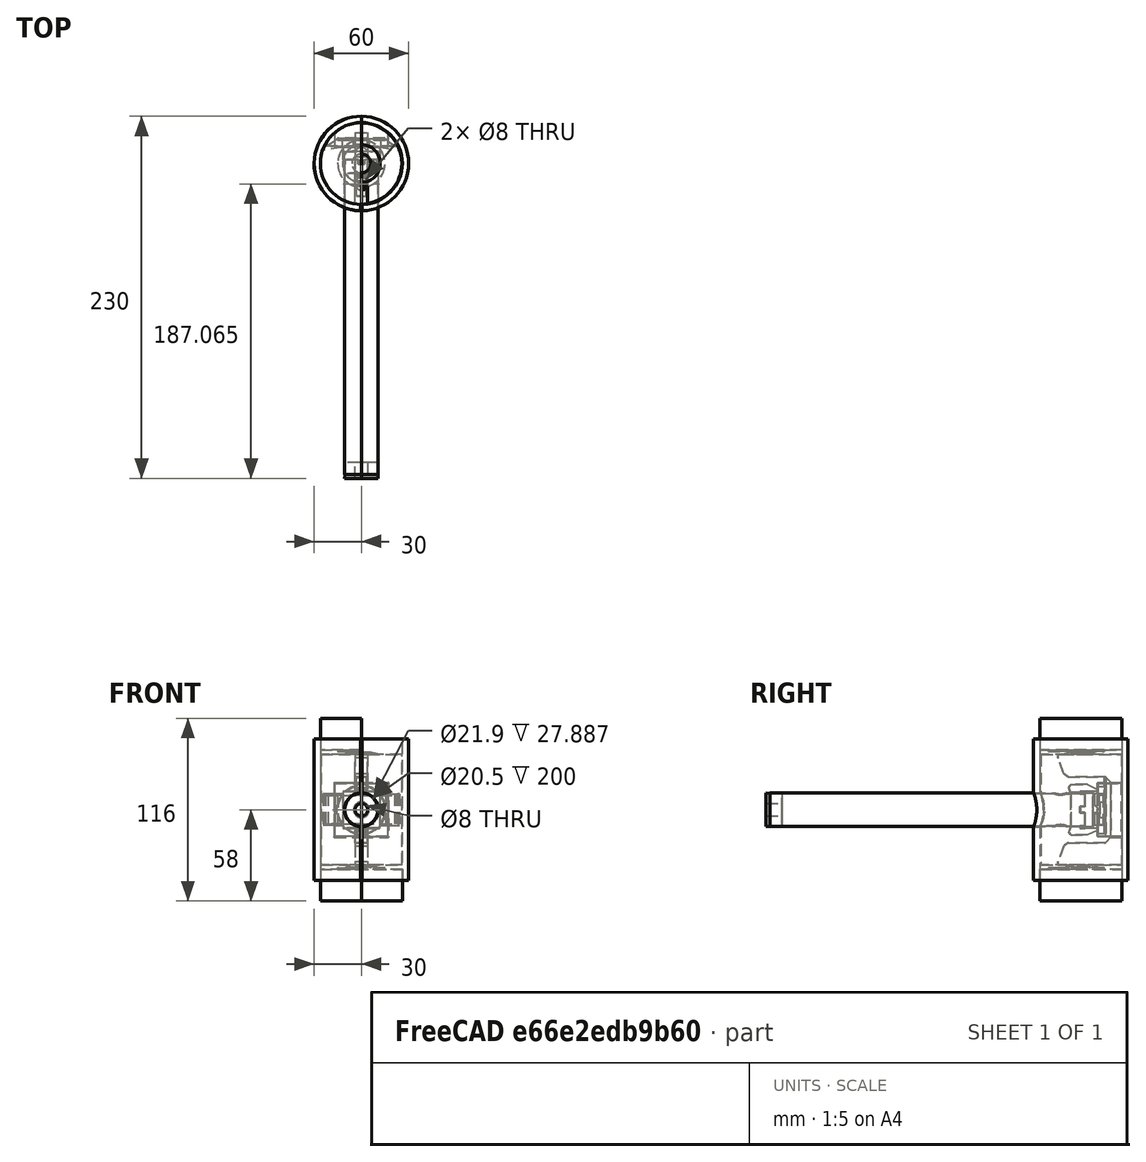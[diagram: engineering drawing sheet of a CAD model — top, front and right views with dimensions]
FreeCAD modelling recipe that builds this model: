
FCSTD DOCUMENT  (FreeCAD 0.21R33771 (Git))
Label: HammerWithDrawings
License: All rights reserved
LicenseURL: https://en.wikipedia.org/wiki/All_rights_reserved
objects: TechDraw::DrawViewDimension×57, Sketcher::SketchObject×26, TechDraw::DrawProjGroupItem×16, PartDesign::Pad×13, PartDesign::Pocket×13, PartDesign::Body×13, App::Link×13, PartDesign::Chamfer×7, TechDraw::DrawSVGTemplate×4, TechDraw::DrawProjGroup×4, TechDraw::DrawPage×4, PartDesign::FeatureBase×3, TechDraw::DrawViewSection×3, PartDesign::AdditiveCone×2, PartDesign::Fillet×2, Spreadsheet::Sheet×1, TechDraw::DrawViewDetail×1, PartDesign::Draft×1, App::DocumentObjectGroupPython×1, Part::FeaturePython×1, +3 more types
note: 216 computed .brp shape members not serialized (recipe doc carries the construction recipe); baked Part::Feature solids carry a one-line shape summary decoded from their .brp

FEATURE [Spreadsheet::Sheet] Spreadsheet  label="Properties"
  cells = A1='PropertyName; B1='Value; A2='Handle_OD; B2(Handle_OD)=21.5; A3='Head_ID; B3(Head_ID)=51.4; A4='Head_Len; B4(Handle_Len)=110; A5='Clearance; B5(Clearance)=0.2; A6='Inset_Len; B6(Insert_Len)=70; A7='Sensor_Wire_Track_Width; B7(Sensor_Wire_Track_Width)=8; A8='Spring_Plate_Len; B8(Spring_Plate_Len)=46; A9='Sensor_Diameter; B9(Sensor_Diameter)=30; A10='Handle_ID; B10(Handle_ID)=20.5
FEATURE [Sketcher::SketchObject] Sketch  label="base"
  FullyConstrained = true
  MapMode = 5
  Support = -> [XY_Plane001]
  expr: Constraints[1] = <<Properties>>.Head_ID
  sketch-geometry (1):
    g0: Circle CenterX=0 CenterY=0 CenterZ=0 NormalX=0 NormalY=0 NormalZ=1 AngleXU=0 Radius=25.7
  constraints (2):
    c: Coincident(g0,g-1)
    c: Diameter(g0) = 51.4
FEATURE [PartDesign::Pad] Pad  label="Base"
  Direction = (0,0,1)
  Length = 35
  Length2 = 35
  Profile = -> Sketch
  ReferenceAxis = -> Sketch [N_Axis]
  Type = 4
  expr: Length = <<Properties>>.Insert_Len / 2
  expr: Length2 = <<Properties>>.Insert_Len / 2
FEATURE [Sketcher::SketchObject] Sketch001  label="sensor_wire_slot"
  FullyConstrained = true
  MapMode = 5
  Support = -> [XY_Plane001]
  expr: Constraints[11] = <<Properties>>.Sensor_Wire_Track_Width
  expr: Constraints[1] = Sketch.Constraints[1]
  sketch-geometry (7):
    g0: Circle CenterX=0 CenterY=0 CenterZ=0 NormalX=0 NormalY=0 NormalZ=1 AngleXU=0 Radius=25.7
    g1: LineSegment StartX=-4 StartY=-25.3868 StartZ=0 EndX=-4 EndY=-14.4568 EndZ=0
    g2: LineSegment StartX=-4 StartY=-14.4568 StartZ=0 EndX=4 EndY=-14.4568 EndZ=0
    g3: LineSegment StartX=4 StartY=-14.4568 StartZ=0 EndX=4 EndY=-25.3868 EndZ=0
    g4: ArcOfCircle CenterX=0 CenterY=0 CenterZ=0 NormalX=0 NormalY=0 NormalZ=1 AngleXU=0 Radius=25.7 StartAngle=4.55611 EndAngle=4.86867
    g5: GeomPoint X=0 Y=-14.4568 Z=0
    g6: Circle CenterX=0 CenterY=0 CenterZ=0 NormalX=0 NormalY=0 NormalZ=1 AngleXU=0 Radius=15
  constraints (17):
    c: Coincident(g0,g-1)
    c: Diameter(g0) = 51.4
    c: Vertical(g1)
    c: Coincident(g2,g1)
    c: Horizontal(g2)
    c: Coincident(g3,g2)
    c: Vertical(g3)
    c: Coincident(g4,g0)
    c: Coincident(g4,g1)
    c: Coincident(g4,g3)
    c: PointOnObject(g3,g0)
    c: DistanceX(g2,g2) = 8
    c: Symmetric(g2,g2,g5)
    c: PointOnObject(g5,g-2)
    c: Coincident(g6,g4)
    c: Diameter(g6) = 30
    c: PointOnObject(g2,g6)
FEATURE [PartDesign::Pocket] Pocket  label="Sensor_Wire_Slot"
  BaseFeature = -> Pad
  Direction = (0,0,-1)
  Length = 35
  Length2 = 35
  Profile = -> Sketch001
  ReferenceAxis = -> Sketch001 [N_Axis]
  Type = 4
  expr: Length = <<Properties>>.Insert_Len / 2
  expr: Length2 = <<Properties>>.Insert_Len / 2
FEATURE [Sketcher::SketchObject] Sketch002  label="handle_hole"
  FullyConstrained = true
  MapMode = 5
  Placement = pos=(0,0,0) rot=(1,0,0;1.5708rad)
  Support = -> [XZ_Plane001]
  expr: Constraints[1] = <<Properties>>.Handle_OD + <<Properties>>.Clearance * 2
  sketch-geometry (1):
    g0: Circle CenterX=0 CenterY=0 CenterZ=0 NormalX=0 NormalY=0 NormalZ=1 AngleXU=0 Radius=10.95
  constraints (2):
    c: Coincident(g0,g-1)
    c: Diameter(g0) = 21.9
FEATURE [PartDesign::Pocket] Pocket001  label="Handle_hole"
  BaseFeature = -> Pocket
  Direction = (0,1,2e-16)
  Length = 25.7
  Length2 = 25.7
  Profile = -> Sketch002
  ReferenceAxis = -> Sketch002 [N_Axis]
  Type = 4
  expr: Length = <<Properties>>.Head_ID / 2
  expr: Length2 = <<Properties>>.Head_ID / 2
FEATURE [Sketcher::SketchObject] Sketch004  label="top_sensor_hole"
  FullyConstrained = true
  MapMode = 5
  Placement = pos=(0,0,0) rot=(0.57735,0.57735,0.57735;2.0944rad)
  Support = -> [YZ_Plane001]
  expr: Constraints[20] = <<Properties>>.Head_ID
  expr: Constraints[7] = <<Properties>>.Sensor_Diameter + 4
  sketch-geometry (9):
    g0: LineSegment StartX=-25.7 StartY=-17 StartZ=0 EndX=-25.7 EndY=17 EndZ=0
    g1: LineSegment StartX=25.7 StartY=17 StartZ=0 EndX=25.7 EndY=-17 EndZ=0
    g2: LineSegment StartX=25.7 StartY=-17 StartZ=0 EndX=-25.7 EndY=-17 EndZ=0
    g3: GeomPoint X=0 Y=0 Z=0
    g4: LineSegment StartX=10.5 StartY=17 StartZ=0 EndX=25.7 EndY=17 EndZ=0
    g5: LineSegment StartX=25.7 StartY=17 StartZ=0 EndX=25.7 EndY=-17 EndZ=0
    g6: LineSegment StartX=25.7 StartY=-17 StartZ=0 EndX=10.5 EndY=-17 EndZ=0
    g7: LineSegment StartX=10.5 StartY=-17 StartZ=0 EndX=10.5 EndY=17 EndZ=0
    g8: LineSegment StartX=-25.7 StartY=17 StartZ=0 EndX=25.7 EndY=17 EndZ=0
  constraints (23):
    c: Coincident(g1,g2)
    c: Coincident(g2,g0)
    c: Horizontal(g2)
    c: Vertical(g0)
    c: Vertical(g1)
    c: Symmetric(g1,g0,g3)
    c: Coincident(g3,g-1)
    c: DistanceY(g1,g1) = 34
    c: Coincident(g4,g5)
    c: Coincident(g5,g6)
    c: Coincident(g6,g7)
    c: Horizontal(g4)
    c: Horizontal(g6)
    c: Vertical(g5)
    c: Vertical(g7)
    c: PointOnObject(g5,g2)
    c: Coincident(g7,g4)
    c: Coincident(g8,g0)
    c: Coincident(g8,g1)
    c: Horizontal(g8)
    c: DistanceX(g8,g8) = 51.4
    c: Coincident(g4,g1)
    c: DistanceX(g3,g4) = 10.5
FEATURE [PartDesign::Pocket] Pocket002  label="Top_Sensor_Hole"
  BaseFeature = -> Pocket001
  Direction = (-1,2e-16,-3e-16)
  Length = 17
  Length2 = 17
  Profile = -> Sketch004
  ReferenceAxis = -> Sketch004 [N_Axis]
  Type = 4
  expr: Length = <<Properties>>.Sensor_Diameter / 2 + 2
  expr: Length2 = <<Properties>>.Sensor_Diameter / 2 + 2
FEATURE [PartDesign::Chamfer] Chamfer
  Angle = 70
  Base = -> Pocket002 [Edge30,Edge32]
  BaseFeature = -> Pocket002
  ChamferType = 2
  FlipDirection = false
  Size = 8
  Size2 = 1
  SupportTransform = false
  UseAllEdges = false
FEATURE [Sketcher::SketchObject] Sketch003  label="spring_plate_slot"
  FullyConstrained = true
  MapMode = 5
  Support = -> [XY_Plane001]
  expr: Constraints[1] = Sketch.Constraints[1]
  expr: Constraints[3] = <<Properties>>.Sensor_Diameter + <<Properties>>.Clearance * 2
  expr: Constraints[7] = <<Properties>>.Spring_Plate_Len
  sketch-geometry (15):
    g0: Circle CenterX=0 CenterY=0 CenterZ=0 NormalX=0 NormalY=0 NormalZ=1 AngleXU=0 Radius=25.7
    g1: LineSegment StartX=-15.2 StartY=15.4669 StartZ=0 EndX=15.2 EndY=15.4669 EndZ=0
    g2: GeomPoint X=0 Y=15.4669 Z=0
    g3: LineSegment StartX=-23 StartY=11.4669 StartZ=0 EndX=23 EndY=11.4669 EndZ=0
    g4: GeomPoint X=0 Y=11.4669 Z=0
    g5: LineSegment StartX=-15.2 StartY=15.4669 StartZ=0 EndX=-21 EndY=11.4669 EndZ=0
    g6: LineSegment StartX=15.2 StartY=15.4669 StartZ=0 EndX=21 EndY=11.4669 EndZ=0
    g7: LineSegment StartX=21 StartY=11.4669 StartZ=0 EndX=23 EndY=11.4669 EndZ=0
    g8: LineSegment StartX=-21 StartY=11.4669 StartZ=0 EndX=-23 EndY=11.4669 EndZ=0
    g9: ArcOfCircle CenterX=0 CenterY=0 CenterZ=0 NormalX=0 NormalY=0 NormalZ=1 AngleXU=0 Radius=25.7 StartAngle=2.6791 EndAngle=2.80587
    g10: ArcOfCircle CenterX=0 CenterY=0 CenterZ=0 NormalX=0 NormalY=0 NormalZ=1 AngleXU=0 Radius=25.7 StartAngle=0.335723 EndAngle=0.462496
    g11: LineSegment StartX=-11 StartY=10.5 StartZ=0 EndX=-24.2652 EndY=8.46691 EndZ=0
    g12: LineSegment StartX=11 StartY=10.5 StartZ=0 EndX=24.2652 EndY=8.46691 EndZ=0
    g13: LineSegment StartX=11 StartY=10.5 StartZ=0 EndX=-11 EndY=10.5 EndZ=0
    g14: GeomPoint X=0 Y=10.5 Z=0
  constraints (39):
    c: Coincident(g0,g-1)
    c: Diameter(g0) = 51.4
    c: Horizontal(g1)
    c: DistanceX(g1,g1) = 30.4
    c: Symmetric(g1,g1,g2)
    c: PointOnObject(g2,g-2)
    c: Horizontal(g3)
    c: DistanceX(g3,g3) = 46
    c: Symmetric(g3,g3,g4)
    c: PointOnObject(g4,g-2)
    c: Coincident(g5,g1)
    c: PointOnObject(g5,g3)
    c: Coincident(g6,g1)
    c: PointOnObject(g6,g3)
    c: Coincident(g7,g6)
    c: PointOnObject(g7,g0)
    c: Horizontal(g7)
    c: Coincident(g8,g5)
    c: PointOnObject(g8,g0)
    c: Horizontal(g8)
    c: Equal(g8,g7)
    c: PointOnObject(g3,g0)
    c: DistanceY(g6,g1) = 4
    c: DistanceX(g6,g7) = 2
    c: Coincident(g9,g0)
    c: Coincident(g9,g8)
    c: Coincident(g10,g9)
    c: Coincident(g10,g7)
    c: Coincident(g13,g12)
    c: Coincident(g13,g11)
    c: Horizontal(g13)
    c: Coincident(g10,g12)
    c: Coincident(g9,g11)
    c: DistanceX(g12,g6) = 10
    c: Equal(g12,g11)
    c: DistanceY(g10,g7) = 3
    c: Symmetric(g13,g13,g14)
    c: PointOnObject(g14,g-2)
    c: DistanceY(g9,g14) = 10.5
FEATURE [PartDesign::Pocket] Pocket003  label="Spring_Plate_Slot"
  BaseFeature = -> Chamfer
  Direction = (0,0,-1)
  Length = 10
  Length2 = 10
  Profile = -> Sketch003
  ReferenceAxis = -> Sketch003 [N_Axis]
  Type = 4
FEATURE [PartDesign::Chamfer] Chamfer001
  Angle = 45
  Base = -> Pocket003 [Edge43,Edge46,Edge45,Edge47,Edge44,Edge42]
  BaseFeature = -> Pocket003
  ChamferType = 0
  FlipDirection = false
  Size = 0.5
  Size2 = 1
  SupportTransform = false
  UseAllEdges = false
FEATURE [Sketcher::SketchObject] Sketch005  label="top_sens_base"
  FullyConstrained = true
  MapMode = 5
  Support = -> [XY_Plane]
  expr: Constraints[18] = <<Properties>>.Clearance
  expr: Constraints[1] = <<Properties>>.Head_ID
  expr: Constraints[3] = 34 - <<Properties>>.Clearance * 2
  expr: Constraints[6] = 10.5 + <<Properties>>.Clearance
  sketch-geometry (8):
    g0: Circle CenterX=0 CenterY=0 CenterZ=0 NormalX=0 NormalY=0 NormalZ=1 AngleXU=0 Radius=25.7
    g1: LineSegment StartX=-16.8 StartY=10.7 StartZ=0 EndX=16.8 EndY=10.7 EndZ=0
    g2: GeomPoint X=0 Y=10.7 Z=0
    g3: LineSegment StartX=-16.8 StartY=10.7 StartZ=0 EndX=-16.8 EndY=19.1836 EndZ=0
    g4: LineSegment StartX=16.8 StartY=10.7 StartZ=0 EndX=16.8 EndY=19.1836 EndZ=0
    g5: GeomPoint X=0 Y=25.7 Z=0
    g6: ArcOfCircle CenterX=0 CenterY=0 CenterZ=0 NormalX=0 NormalY=0 NormalZ=1 AngleXU=0 Radius=25.5 StartAngle=0.851542 EndAngle=2.29005
    g7: GeomPoint X=0 Y=25.5 Z=0
  constraints (19):
    c: Coincident(g0,g-1)
    c: Diameter(g0) = 51.4
    c: Horizontal(g1)
    c: DistanceX(g1,g1) = 33.6
    c: Symmetric(g1,g1,g2)
    c: PointOnObject(g2,g-2)
    c: DistanceY(g0,g2) = 10.7
    c: Coincident(g3,g1)
    c: Vertical(g3)
    c: Vertical(g4)
    c: Coincident(g4,g1)
    c: PointOnObject(g5,g0)
    c: PointOnObject(g5,g-2)
    c: Coincident(g6,g0)
    c: Coincident(g6,g3)
    c: Coincident(g6,g4)
    c: PointOnObject(g7,g6)
    c: PointOnObject(g7,g-2)
    c: DistanceY(g7,g5) = 0.2
FEATURE [PartDesign::Pad] Pad001  label="Top_Base"
  Direction = (0,0,1)
  Length = 16.8
  Length2 = 16.8
  Profile = -> Sketch005
  ReferenceAxis = -> Sketch005 [N_Axis]
  Type = 4
  expr: Length = <<Properties>>.Sensor_Diameter / 2 + 2 - <<Properties>>.Clearance
  expr: Length2 = <<Properties>>.Sensor_Diameter / 2 + 2 - <<Properties>>.Clearance
FEATURE [Sketcher::SketchObject] Sketch006
  FullyConstrained = true
  MapMode = 5
  Support = -> [XY_Plane]
  expr: Constraints[1] = Sketch003.Constraints[1]
  expr: Constraints[22] = Sketch003.Constraints[22]
  expr: Constraints[23] = Sketch003.Constraints[23]
  expr: Constraints[33] = Sketch003.Constraints[33]
  expr: Constraints[35] = Sketch003.Constraints[35]
  expr: Constraints[38] = Sketch003.Constraints[38]
  expr: Constraints[3] = Sketch003.Constraints[3]
  expr: Constraints[7] = Sketch003.Constraints[7]
  sketch-geometry (15):
    g0: Circle CenterX=0 CenterY=0 CenterZ=0 NormalX=0 NormalY=0 NormalZ=1 AngleXU=0 Radius=25.7
    g1: LineSegment StartX=-15.2 StartY=15.4669 StartZ=0 EndX=15.2 EndY=15.4669 EndZ=0
    g2: GeomPoint X=0 Y=15.4669 Z=0
    g3: LineSegment StartX=-23 StartY=11.4669 StartZ=0 EndX=23 EndY=11.4669 EndZ=0
    g4: GeomPoint X=0 Y=11.4669 Z=0
    g5: LineSegment StartX=-15.2 StartY=15.4669 StartZ=0 EndX=-21 EndY=11.4669 EndZ=0
    g6: LineSegment StartX=15.2 StartY=15.4669 StartZ=0 EndX=21 EndY=11.4669 EndZ=0
    g7: LineSegment StartX=21 StartY=11.4669 StartZ=0 EndX=23 EndY=11.4669 EndZ=0
    g8: LineSegment StartX=-21 StartY=11.4669 StartZ=0 EndX=-23 EndY=11.4669 EndZ=0
    g9: ArcOfCircle CenterX=0 CenterY=0 CenterZ=0 NormalX=0 NormalY=0 NormalZ=1 AngleXU=0 Radius=25.7 StartAngle=2.6791 EndAngle=2.80587
    g10: ArcOfCircle CenterX=0 CenterY=0 CenterZ=0 NormalX=0 NormalY=0 NormalZ=1 AngleXU=0 Radius=25.7 StartAngle=0.335723 EndAngle=0.462496
    g11: LineSegment StartX=-11 StartY=10.5 StartZ=0 EndX=-24.2652 EndY=8.46691 EndZ=0
    g12: LineSegment StartX=11 StartY=10.5 StartZ=0 EndX=24.2652 EndY=8.46691 EndZ=0
    g13: LineSegment StartX=11 StartY=10.5 StartZ=0 EndX=-11 EndY=10.5 EndZ=0
    g14: GeomPoint X=0 Y=10.5 Z=0
  constraints (40):
    c: Coincident(g0,g-1)
    c: Diameter(g0) = 51.4
    c: Horizontal(g1)
    c: DistanceX(g1,g1) = 30.4
    c: Symmetric(g1,g1,g2)
    c: PointOnObject(g2,g-2)
    c: Horizontal(g3)
    c: DistanceX(g3,g3) = 46
    c: Symmetric(g3,g3,g4)
    c: PointOnObject(g4,g-2)
    c: Coincident(g5,g1)
    c: PointOnObject(g5,g3)
    c: Coincident(g6,g1)
    c: PointOnObject(g6,g3)
    c: Coincident(g7,g6)
    c: PointOnObject(g7,g0)
    c: Horizontal(g7)
    c: Coincident(g8,g5)
    c: PointOnObject(g8,g0)
    c: Horizontal(g8)
    c: Equal(g8,g7)
    c: PointOnObject(g3,g0)
    c: DistanceY(g6,g1) = 4
    c: DistanceX(g6,g7) = 2
    c: Coincident(g9,g0)
    c: Coincident(g9,g8)
    c: Coincident(g10,g9)
    c: Coincident(g10,g7)
    c: Coincident(g13,g12)
    c: Coincident(g13,g11)
    c: Horizontal(g13)
    c: Coincident(g10,g12)
    c: Coincident(g9,g11)
    c: DistanceX(g12,g6) = 10
    c: Equal(g12,g11)
    c: DistanceY(g10,g7) = 3
    c: Symmetric(g13,g13,g14)
    c: PointOnObject(g14,g-2)
    c: DistanceY(g9,g14) = 10.5
    c: DistanceY(g9,g2) = 15.4669
FEATURE [PartDesign::Pocket] Pocket004
  BaseFeature = -> Pad001
  Direction = (0,0,-1)
  Length = 9.5
  Length2 = 9.5
  Profile = -> Sketch006
  ReferenceAxis = -> Sketch006 [N_Axis]
  Type = 4
FEATURE [PartDesign::Chamfer] Chamfer002
  Angle = 45
  Base = -> Pocket004 [Edge22,Edge12]
  BaseFeature = -> Pocket004
  ChamferType = 0
  FlipDirection = false
  Size = 0.3
  Size2 = 1
  SupportTransform = false
  UseAllEdges = false
FEATURE [Sketcher::SketchObject] Sketch007
  FullyConstrained = true
  MapMode = 5
  Placement = pos=(0,0,0) rot=(1,0,0;1.5708rad)
  Support = -> [XZ_Plane]
  expr: Constraints[11] = <<Properties>>.Sensor_Wire_Track_Width
  expr: Constraints[1] = <<Properties>>.Sensor_Diameter + 1
  expr: Constraints[27] = <<Properties>>.Sensor_Wire_Track_Width
  sketch-geometry (11):
    g0: Circle CenterX=0 CenterY=0 CenterZ=0 NormalX=0 NormalY=0 NormalZ=1 AngleXU=0 Radius=15.5
    g1: LineSegment StartX=-4 StartY=14.975 StartZ=0 EndX=-4 EndY=27.305 EndZ=0
    g2: LineSegment StartX=-4 StartY=27.305 StartZ=0 EndX=4 EndY=27.305 EndZ=0
    g3: LineSegment StartX=4 StartY=27.305 StartZ=0 EndX=4 EndY=14.975 EndZ=0
    g4: GeomPoint X=0 Y=27.305 Z=0
    g5: LineSegment StartX=-4 StartY=-14.975 StartZ=0 EndX=-4 EndY=-27.305 EndZ=0
    g6: LineSegment StartX=-4 StartY=-27.305 StartZ=0 EndX=4 EndY=-27.305 EndZ=0
    g7: LineSegment StartX=4 StartY=-27.305 StartZ=0 EndX=4 EndY=-14.975 EndZ=0
    g8: GeomPoint X=0 Y=-27.305 Z=0
    g9: ArcOfCircle CenterX=0 CenterY=0 CenterZ=0 NormalX=0 NormalY=0 NormalZ=1 AngleXU=0 Radius=15.5 StartAngle=1.83181 EndAngle=4.45137
    g10: ArcOfCircle CenterX=0 CenterY=0 CenterZ=0 NormalX=0 NormalY=0 NormalZ=1 AngleXU=0 Radius=15.5 StartAngle=4.97341 EndAngle=7.59296
  constraints (28):
    c: Coincident(g0,g-1)
    c: Diameter(g0) = 31
    c: PointOnObject(g1,g0)
    c: Vertical(g1)
    c: Coincident(g2,g1)
    c: Horizontal(g2)
    c: Coincident(g3,g2)
    c: PointOnObject(g3,g0)
    c: Vertical(g3)
    c: Symmetric(g2,g2,g4)
    c: PointOnObject(g4,g-2)
    c: DistanceX(g2,g2) = 8
    c: DistanceY(g3,g3) = 12.33
    c: Vertical(g5)
    c: Coincident(g6,g5)
    c: Horizontal(g6)
    c: Coincident(g7,g6)
    c: Vertical(g7)
    c: Symmetric(g6,g6,g8)
    c: PointOnObject(g8,g-2)
    c: Equal(g7,g3)
    c: Coincident(g9,g0)
    c: Coincident(g9,g1)
    c: Coincident(g9,g5)
    c: Coincident(g10,g9)
    c: Coincident(g10,g3)
    c: Coincident(g10,g7)
    c: DistanceX(g6,g6) = 8
FEATURE [PartDesign::Pocket] Pocket005
  BaseFeature = -> Chamfer002
  Direction = (0,1,2e-16)
  Length = 0
  Length2 = 5
  Offset = 0.4
  Profile = -> Sketch007
  ReferenceAxis = -> Sketch007 [N_Axis]
  Type = 3
  UpToFace = -> Chamfer002 [Face11]
FEATURE [PartDesign::Body] Body001  label="TopSensor"
  Group = -> [Sketch005,Pad001,Sketch006,Pocket004,Chamfer002,Sketch007,Pocket005]
  Origin = -> Origin
  Tip = -> Pocket005
FEATURE [Sketcher::SketchObject] Sketch008
  FullyConstrained = true
  MapMode = 5
  Placement = pos=(0,0,0) rot=(0.57735,0.57735,0.57735;2.0944rad)
  Support = -> [YZ_Plane001]
  expr: Constraints[16] = <<Properties>>.Sensor_Diameter + 2
  sketch-geometry (14):
    g0: LineSegment StartX=15.5 StartY=21 StartZ=0 EndX=15.5 EndY=-21 EndZ=0
    g1: LineSegment StartX=15.5 StartY=-21 StartZ=0 EndX=-19.02 EndY=-21 EndZ=0
    g2: LineSegment StartX=-19.02 StartY=-21 StartZ=0 EndX=-19.02 EndY=-16 EndZ=0
    g3: LineSegment StartX=-19.02 StartY=-16 StartZ=0 EndX=10.5 EndY=-16 EndZ=0
    g4: LineSegment StartX=10.5 StartY=-16 StartZ=0 EndX=10.5 EndY=16 EndZ=0
    g5: LineSegment StartX=10.5 StartY=16 StartZ=0 EndX=-19.02 EndY=16 EndZ=0
    g6: LineSegment StartX=-19.02 StartY=16 StartZ=0 EndX=-19.02 EndY=21 EndZ=0
    g7: LineSegment StartX=-19.02 StartY=21 StartZ=0 EndX=15.5 EndY=21 EndZ=0
    g8: GeomPoint X=10.5 Y=0 Z=0
    g9: GeomPoint X=15.5 Y=0 Z=0
    g10: GeomPoint X=15.5 Y=21 Z=0
    g11: GeomPoint X=15.5 Y=-21 Z=0
    g12: GeomPoint X=10.5 Y=16 Z=0
    g13: GeomPoint X=10.5 Y=-16 Z=0
  constraints (30):
    c: Vertical(g0)
    c: Horizontal(g1)
    c: Coincident(g2,g1)
    c: Vertical(g2)
    c: Coincident(g3,g2)
    c: Horizontal(g3)
    c: Vertical(g4)
    c: Horizontal(g5)
    c: Coincident(g6,g5)
    c: Vertical(g6)
    c: Coincident(g7,g6)
    c: Horizontal(g7)
    c: Symmetric(g10,g11,g9)
    c: Symmetric(g13,g12,g8)
    c: PointOnObject(g8,g-1)
    c: PointOnObject(g9,g-1)
    c: DistanceY(g13,g12) = 32
    c: DistanceY(g6,g6) = 5
    c: DistanceX(g8,g9) = 5
    c: DistanceX(g-1,g8) = 10.5
    c: DistanceX(g7,g10) = 34.52
    c: Coincident(g0,g10)
    c: Coincident(g7,g0)
    c: Coincident(g4,g12)
    c: Coincident(g5,g4)
    c: Coincident(g0,g11)
    c: Coincident(g4,g13)
    c: Coincident(g3,g4)
    c: Coincident(g1,g0)
    c: Equal(g3,g5)
FEATURE [PartDesign::Pocket] Pocket006
  BaseFeature = -> Chamfer001
  Direction = (-1,2e-16,-3e-16)
  Length = 4
  Length2 = 4
  Profile = -> Sketch008
  ReferenceAxis = -> Sketch008 [N_Axis]
  Type = 4
  expr: Length = <<Properties>>.Sensor_Wire_Track_Width / 2
  expr: Length2 = <<Properties>>.Sensor_Wire_Track_Width / 2
FEATURE [PartDesign::Chamfer] Chamfer003
  Angle = 65
  Base = -> Pocket006 [Edge148,Edge154]
  BaseFeature = -> Pocket006
  ChamferType = 2
  FlipDirection = false
  Size = 3
  Size2 = 1
  SupportTransform = false
  UseAllEdges = false
FEATURE [PartDesign::Chamfer] Chamfer004
  Angle = 45
  Base = -> Chamfer003 [Edge167,Edge85,Edge52,Edge56]
  BaseFeature = -> Chamfer003
  ChamferType = 0
  FlipDirection = false
  Size = 2
  Size2 = 1
  SupportTransform = false
  UseAllEdges = false
FEATURE [PartDesign::Chamfer] Chamfer005
  Angle = 45
  Base = -> Chamfer004 [Edge169,Edge38]
  BaseFeature = -> Chamfer004
  ChamferType = 1
  FlipDirection = false
  Size = 4
  Size2 = 3.999
  SupportTransform = false
  UseAllEdges = false
FEATURE [Sketcher::SketchObject] Sketch009
  FullyConstrained = true
  MapMode = 5
  Support = -> [XY_Plane002]
  sketch-geometry (2):
    g0: Circle CenterX=0 CenterY=0 CenterZ=0 NormalX=0 NormalY=0 NormalZ=1 AngleXU=0 Radius=26
    g1: Circle CenterX=0 CenterY=0 CenterZ=0 NormalX=0 NormalY=0 NormalZ=1 AngleXU=0 Radius=30
  constraints (4):
    c: Coincident(g0,g-1)
    c: Coincident(g1,g0)
    c: Diameter(g0) = 52
    c: Diameter(g1) = 60
FEATURE [PartDesign::Pad] Pad002
  Direction = (0,0,1)
  Length = 45
  Length2 = 45
  Profile = -> Sketch009
  ReferenceAxis = -> Sketch009 [N_Axis]
  Type = 4
FEATURE [Sketcher::SketchObject] Sketch010
  FullyConstrained = true
  MapMode = 5
  Placement = pos=(0,0,0) rot=(1,0,0;1.5708rad)
  Support = -> [XZ_Plane002]
  expr: Constraints[1] = <<Properties>>.Handle_OD
  sketch-geometry (1):
    g0: Circle CenterX=0 CenterY=0 CenterZ=0 NormalX=0 NormalY=0 NormalZ=1 AngleXU=0 Radius=10.75
  constraints (2):
    c: Coincident(g0,g-1)
    c: Diameter(g0) = 21.5
FEATURE [PartDesign::Pocket] Pocket007
  BaseFeature = -> Pad002
  Direction = (0,1,2e-16)
  Length = 5
  Length2 = 5
  Profile = -> Sketch010
  ReferenceAxis = -> Sketch010 [N_Axis]
  Reversed = true
  Type = 1
FEATURE [Sketcher::SketchObject] Sketch011
  FullyConstrained = true
  MapMode = 5
  Placement = pos=(0,0,0) rot=(1,0,0;1.5708rad)
  Support = -> [XZ_Plane003]
  expr: Constraints[3] = <<Properties>>.Handle_ID
  sketch-geometry (2):
    g0: Circle CenterX=0 CenterY=0 CenterZ=0 NormalX=0 NormalY=0 NormalZ=1 AngleXU=0 Radius=10.625
    g1: Circle CenterX=0 CenterY=0 CenterZ=0 NormalX=0 NormalY=0 NormalZ=1 AngleXU=0 Radius=10.25
  constraints (4):
    c: Coincident(g0,g-1)
    c: Diameter(g0) = 21.25
    c: Coincident(g1,g0)
    c: Diameter(g1) = 20.5
FEATURE [PartDesign::Pad] Pad003
  Direction = (0,-1,-2e-16)
  Length = 200
  Length2 = 10
  Placement = pos=(0,0,0) rot=(1,0,0;1.5708rad)
  Profile = -> Sketch011
  ReferenceAxis = -> Sketch011 [N_Axis]
  Type = 0
FEATURE [Sketcher::SketchObject] Sketch014
  FullyConstrained = true
  MapMode = 5
  Support = -> [XY_Plane005]
  sketch-geometry (5):
    g0: ArcOfCircle CenterX=0 CenterY=0 CenterZ=0 NormalX=0 NormalY=0 NormalZ=1 AngleXU=0 Radius=15 StartAngle=4.90695 EndAngle=10.801
    g1: LineSegment StartX=2.9 StartY=-14.717 StartZ=0 EndX=2.9 EndY=-20.717 EndZ=0
    g2: LineSegment StartX=2.9 StartY=-20.717 StartZ=0 EndX=-2.9 EndY=-20.717 EndZ=0
    g3: LineSegment StartX=-2.9 StartY=-20.717 StartZ=0 EndX=-2.9 EndY=-14.717 EndZ=0
    g4: LineSegment StartX=2.9 StartY=-14.717 StartZ=0 EndX=-2.9 EndY=-14.717 EndZ=0
  constraints (14):
    c: Coincident(g0,g-1)
    c: Radius(g0) = 15
    c: Coincident(g1,g0)
    c: Vertical(g1)
    c: Coincident(g2,g1)
    c: Horizontal(g2)
    c: Coincident(g3,g2)
    c: Coincident(g3,g0)
    c: Vertical(g3)
    c: DistanceX(g2,g2) = 5.8
    c: Coincident(g4,g0)
    c: Coincident(g4,g0)
    c: Horizontal(g4)
    c: DistanceY(g1,g1) = 6
FEATURE [PartDesign::Pad] Pad007
  Direction = (0,0,1)
  Length = 1
  Length2 = 10
  Profile = -> Sketch014
  ReferenceAxis = -> Sketch014 [N_Axis]
  Type = 0
FEATURE [PartDesign::Body] Body005  label="Sensor1"
  Group = -> [Sketch014,Pad007]
  Origin = -> Origin005
  Placement = pos=(0,0,37) rot=(0,0,1;0rad)
  Tip = -> Pad007
FEATURE [PartDesign::FeatureBase] Clone
  BaseFeature = -> Body005
FEATURE [PartDesign::Body] Body006  label="Sensor2"
  Group = -> [Clone]
  Origin = -> Origin006
  Placement = pos=(0,0,-37) rot=(0,1,0;3.14159rad)
  Tip = -> Clone
FEATURE [PartDesign::FeatureBase] Clone001
  BaseFeature = -> Body005
FEATURE [PartDesign::Body] Body007  label="Sensor3"
  Group = -> [Clone001]
  Origin = -> Origin007
  Placement = pos=(0,16,-4e-15) rot=(0,0.707107,-0.707107;3.14159rad)
  Tip = -> Clone001
FEATURE [PartDesign::AdditiveCone] Cone
  Angle = 360
  AttacherType = Attacher::AttachEngine3D
  BaseFeature = -> Chamfer005
  Height = 1.5
  MapMode = 5
  Placement = pos=(0,0,35) rot=(0,0,1;0rad)
  Radius1 = 12
  Radius2 = 6
  Support = -> [Chamfer005]
FEATURE [PartDesign::AdditiveCone] Cone001
  Angle = 360
  AttacherType = Attacher::AttachEngine3D
  BaseFeature = -> Cone
  Height = 1.5
  MapMode = 5
  Placement = pos=(0,0,-35) rot=(1,0,0;3.14159rad)
  Radius1 = 12
  Radius2 = 6
  Support = -> [Cone]
FEATURE [Sketcher::SketchObject] Sketch015
  FullyConstrained = true
  MapMode = 5
  Support = -> [XY_Plane008]
  sketch-geometry (1):
    g0: Circle CenterX=0 CenterY=0 CenterZ=0 NormalX=0 NormalY=0 NormalZ=1 AngleXU=0 Radius=26
  constraints (2):
    c: Coincident(g0,g-1)
    c: Diameter(g0) = 52
FEATURE [PartDesign::Pad] Pad008
  Direction = (0,0,1)
  Length = 20
  Length2 = 10
  Profile = -> Sketch015
  ReferenceAxis = -> Sketch015 [N_Axis]
  Type = 0
FEATURE [PartDesign::Body] Body008  label="Foam1"
  Group = -> [Sketch015,Pad008]
  Origin = -> Origin008
  Placement = pos=(0,0,38) rot=(0,0,1;0rad)
  Tip = -> Pad008
FEATURE [PartDesign::FeatureBase] Clone002
  BaseFeature = -> Body008
  Placement = pos=(0,0,38) rot=(0,0,1;0rad)
FEATURE [PartDesign::Body] Body009  label="Foam2"
  Group = -> [Clone002]
  Origin = -> Origin009
  Placement = pos=(0,0,0) rot=(1,0,0;3.14159rad)
  Tip = -> Clone002
FEATURE [Sketcher::SketchObject] Sketch016
  FullyConstrained = true
  MapMode = 5
  Support = -> [XY_Plane010]
  sketch-geometry (5):
    g0: LineSegment StartX=-22.5 StartY=-0.4 StartZ=0 EndX=-22.5 EndY=0.4 EndZ=0
    g1: LineSegment StartX=-22.5 StartY=0.4 StartZ=0 EndX=22.5 EndY=0.4 EndZ=0
    g2: LineSegment StartX=22.5 StartY=0.4 StartZ=0 EndX=22.5 EndY=-0.4 EndZ=0
    g3: LineSegment StartX=22.5 StartY=-0.4 StartZ=0 EndX=-22.5 EndY=-0.4 EndZ=0
    g4: GeomPoint X=0 Y=0 Z=0
  constraints (12):
    c: Coincident(g0,g1)
    c: Coincident(g1,g2)
    c: Coincident(g2,g3)
    c: Coincident(g3,g0)
    c: Horizontal(g1)
    c: Horizontal(g3)
    c: Vertical(g0)
    c: Vertical(g2)
    c: Symmetric(g1,g0,g4)
    c: Coincident(g4,g-1)
    c: DistanceX(g1,g1) = 45
    c: DistanceY(g2,g2) = 0.8
FEATURE [PartDesign::Pad] Pad009
  Direction = (0,0,1)
  Length = 9
  Length2 = 9
  Profile = -> Sketch016
  ReferenceAxis = -> Sketch016 [N_Axis]
  Type = 4
FEATURE [PartDesign::Body] Body010  label="ShimStock"
  Group = -> [Sketch016,Pad009]
  Origin = -> Origin010
  Placement = pos=(0,11,0) rot=(0,0,1;0rad)
  Tip = -> Pad009
FEATURE [Sketcher::SketchObject] Sketch017
  FullyConstrained = true
  MapMode = 5
  Placement = pos=(0,0,0) rot=(1,0,0;1.5708rad)
  Support = -> [XZ_Plane011]
  sketch-geometry (1):
    g0: Circle CenterX=0 CenterY=0 CenterZ=0 NormalX=0 NormalY=0 NormalZ=1 AngleXU=0 Radius=5
  constraints (2):
    c: Coincident(g0,g-1)
    c: Diameter(g0) = 10
FEATURE [PartDesign::Pad] Pad010
  Direction = (0,-1,-2e-16)
  Length = 3
  Length2 = 10
  Placement = pos=(0,0,0) rot=(1,0,0;1.5708rad)
  Profile = -> Sketch017
  ReferenceAxis = -> Sketch017 [N_Axis]
  Type = 0
FEATURE [PartDesign::Body] Body011  label="TopFoam"
  Group = -> [Sketch017,Pad010]
  Origin = -> Origin011
  Placement = pos=(0,15,0) rot=(0,0,1;0rad)
  Tip = -> Pad010
FEATURE [Sketcher::SketchObject] Sketch018
  FullyConstrained = false
  MapMode = 5
  Support = -> [XY_Plane003]
  sketch-geometry (1):
    g0: Circle CenterX=0 CenterY=-15.4348 CenterZ=0 NormalX=0 NormalY=0 NormalZ=1 AngleXU=0 Radius=4
  constraints (2):
    c: PointOnObject(g0,g-2)
    c: Diameter(g0) = 8
FEATURE [PartDesign::Pocket] Pocket008
  BaseFeature = -> Pad003
  Direction = (0,0,-1)
  Length = 50
  Length2 = 50
  Placement = pos=(0,0,0) rot=(1,0,0;1.5708rad)
  Profile = -> Sketch018
  ReferenceAxis = -> Sketch018 [N_Axis]
  Type = 4
FEATURE [Sketcher::SketchObject] Sketch019
  FullyConstrained = true
  MapMode = 5
  Placement = pos=(0,0,0) rot=(1,0,0;1.5708rad)
  Support = -> [XZ_Plane003]
  sketch-geometry (17):
    g0: LineSegment StartX=12 StartY=-2 StartZ=0 EndX=12 EndY=2 EndZ=0
    g1: LineSegment StartX=12 StartY=2 StartZ=0 EndX=2 EndY=2 EndZ=0
    g2: LineSegment StartX=2 StartY=2 StartZ=0 EndX=2 EndY=12 EndZ=0
    g3: LineSegment StartX=2 StartY=12 StartZ=0 EndX=-2 EndY=12 EndZ=0
    g4: LineSegment StartX=-2 StartY=12 StartZ=0 EndX=-2 EndY=2 EndZ=0
    g5: LineSegment StartX=-2 StartY=2 StartZ=0 EndX=-12 EndY=2 EndZ=0
    g6: LineSegment StartX=-12 StartY=2 StartZ=0 EndX=-12 EndY=-2 EndZ=0
    g7: LineSegment StartX=-12 StartY=-2 StartZ=0 EndX=-2 EndY=-2 EndZ=0
    g8: LineSegment StartX=-2 StartY=-2 StartZ=0 EndX=-2 EndY=-12 EndZ=0
    g9: LineSegment StartX=-2 StartY=-12 StartZ=0 EndX=2 EndY=-12 EndZ=0
    g10: LineSegment StartX=2 StartY=-12 StartZ=0 EndX=2 EndY=-2 EndZ=0
    g11: LineSegment StartX=2 StartY=-2 StartZ=0 EndX=12 EndY=-2 EndZ=0
    g12: LineSegment StartX=-2 StartY=-2 StartZ=0 EndX=-2 EndY=2 EndZ=0
    g13: LineSegment StartX=-2 StartY=2 StartZ=0 EndX=2 EndY=2 EndZ=0
    g14: LineSegment StartX=2 StartY=2 StartZ=0 EndX=2 EndY=-2 EndZ=0
    g15: LineSegment StartX=2 StartY=-2 StartZ=0 EndX=-2 EndY=-2 EndZ=0
    g16: GeomPoint X=0 Y=0 Z=0
  constraints (46):
    c: Vertical(g0)
    c: Coincident(g1,g0)
    c: Horizontal(g1)
    c: Coincident(g2,g1)
    c: Vertical(g2)
    c: Coincident(g3,g2)
    c: Horizontal(g3)
    c: Coincident(g4,g3)
    c: Vertical(g4)
    c: Coincident(g5,g4)
    c: Horizontal(g5)
    c: Coincident(g6,g5)
    c: Vertical(g6)
    c: Horizontal(g7)
    c: Coincident(g8,g7)
    c: Vertical(g8)
    c: Horizontal(g9)
    c: Coincident(g10,g9)
    c: Vertical(g10)
    c: Coincident(g11,g10)
    c: Coincident(g11,g0)
    c: Horizontal(g11)
    c: Equal(g0,g3)
    c: Equal(g3,g6)
    c: Equal(g6,g9)
    c: Coincident(g6,g7)
    c: Coincident(g9,g8)
    c: Equal(g11,g7)
    c: Equal(g11,g1)
    c: Equal(g2,g4)
    c: Equal(g5,g10)
    c: Coincident(g12,g13)
    c: Coincident(g13,g14)
    c: Coincident(g14,g15)
    c: Coincident(g15,g12)
    c: Horizontal(g13)
    c: Horizontal(g15)
    c: Vertical(g12)
    c: Vertical(g14)
    c: Symmetric(g13,g12,g16)
    c: Coincident(g16,g-1)
    c: Coincident(g13,g1)
    c: Coincident(g7,g12)
    c: DistanceX(g13,g13) = 4
    c: DistanceY(g2,g2) = 10
    c: Equal(g10,g2)
FEATURE [PartDesign::Pocket] Pocket009
  BaseFeature = -> Pocket008
  Direction = (0,1,2e-16)
  Length = 3
  Length2 = 5
  Placement = pos=(0,0,0) rot=(1,0,0;1.5708rad)
  Profile = -> Sketch019
  ReferenceAxis = -> Sketch019 [N_Axis]
  Reversed = true
  Type = 0
FEATURE [PartDesign::Body] Body003  label="MetalHandle"
  Group = -> [Sketch011,Pad003,Sketch018,Pocket008,Sketch019,Pocket009]
  Origin = -> Origin003
  Placement = pos=(0,2.5,0) rot=(0,0,1;0rad)
  Tip = -> Pocket009
FEATURE [Sketcher::SketchObject] Sketch020
  FullyConstrained = true
  MapMode = 5
  Placement = pos=(0,0,0) rot=(1,0,0;1.5708rad)
  Support = -> [XZ_Plane012]
  expr: Constraints[43] = Sketch019.Constraints[43]
  expr: Constraints[44] = Sketch019.Constraints[44]
  expr: Constraints[77] = <<Properties>>.Clearance
  expr: Constraints[78] = <<Properties>>.Clearance
  expr: Constraints[79] = <<Properties>>.Clearance
  expr: Constraints[81] = (<<Properties>>.Handle_OD + 2) / 2 - <<Properties>>.Clearance
  sketch-geometry (29):
    g0: LineSegment StartX=12 StartY=-2 StartZ=0 EndX=12 EndY=2 EndZ=0
    g1: LineSegment StartX=12 StartY=2 StartZ=0 EndX=2 EndY=2 EndZ=0
    g2: LineSegment StartX=2 StartY=2 StartZ=0 EndX=2 EndY=12 EndZ=0
    g3: LineSegment StartX=2 StartY=12 StartZ=0 EndX=-2 EndY=12 EndZ=0
    g4: LineSegment StartX=-2 StartY=12 StartZ=0 EndX=-2 EndY=2 EndZ=0
    g5: LineSegment StartX=-2 StartY=2 StartZ=0 EndX=-12 EndY=2 EndZ=0
    g6: LineSegment StartX=-12 StartY=2 StartZ=0 EndX=-12 EndY=-2 EndZ=0
    g7: LineSegment StartX=-12 StartY=-2 StartZ=0 EndX=-2 EndY=-2 EndZ=0
    g8: LineSegment StartX=-2 StartY=-2 StartZ=0 EndX=-2 EndY=-12 EndZ=0
    g9: LineSegment StartX=-2 StartY=-12 StartZ=0 EndX=2 EndY=-12 EndZ=0
    g10: LineSegment StartX=2 StartY=-12 StartZ=0 EndX=2 EndY=-2 EndZ=0
    g11: LineSegment StartX=2 StartY=-2 StartZ=0 EndX=12 EndY=-2 EndZ=0
    g12: LineSegment StartX=-2 StartY=-2 StartZ=0 EndX=-2 EndY=2 EndZ=0
    g13: LineSegment StartX=-2 StartY=2 StartZ=0 EndX=2 EndY=2 EndZ=0
    g14: LineSegment StartX=2 StartY=2 StartZ=0 EndX=2 EndY=-2 EndZ=0
    g15: LineSegment StartX=2 StartY=-2 StartZ=0 EndX=-2 EndY=-2 EndZ=0
    g16: GeomPoint X=0 Y=0 Z=0
    g17: LineSegment StartX=-1.8 StartY=11.55 StartZ=0 EndX=-1.8 EndY=1.8 EndZ=0
    g18: LineSegment StartX=-1.8 StartY=1.8 StartZ=0 EndX=-11.55 EndY=1.8 EndZ=0
    g19: LineSegment StartX=-11.55 StartY=1.8 StartZ=0 EndX=-11.55 EndY=-1.8 EndZ=0
    g20: LineSegment StartX=-11.55 StartY=-1.8 StartZ=0 EndX=-1.8 EndY=-1.8 EndZ=0
    g21: LineSegment StartX=-1.8 StartY=-1.8 StartZ=0 EndX=-1.8 EndY=-11.55 EndZ=0
    g22: LineSegment StartX=-1.8 StartY=-11.55 StartZ=0 EndX=1.8 EndY=-11.55 EndZ=0
    g23: LineSegment StartX=1.8 StartY=-11.55 StartZ=0 EndX=1.8 EndY=-1.8 EndZ=0
    g24: LineSegment StartX=1.8 StartY=-1.8 StartZ=0 EndX=11.55 EndY=-1.8 EndZ=0
    g25: LineSegment StartX=11.55 StartY=-1.8 StartZ=0 EndX=11.55 EndY=1.8 EndZ=0
    g26: LineSegment StartX=11.55 StartY=1.8 StartZ=0 EndX=1.8 EndY=1.8 EndZ=0
    g27: LineSegment StartX=1.8 StartY=1.8 StartZ=0 EndX=1.8 EndY=11.55 EndZ=0
    g28: LineSegment StartX=1.8 StartY=11.55 StartZ=0 EndX=-1.8 EndY=11.55 EndZ=0
  constraints (82):
    c: Vertical(g0)
    c: Coincident(g1,g0)
    c: Horizontal(g1)
    c: Coincident(g2,g1)
    c: Vertical(g2)
    c: Coincident(g3,g2)
    c: Horizontal(g3)
    c: Coincident(g4,g3)
    c: Vertical(g4)
    c: Coincident(g5,g4)
    c: Horizontal(g5)
    c: Coincident(g6,g5)
    c: Vertical(g6)
    c: Horizontal(g7)
    c: Coincident(g8,g7)
    c: Vertical(g8)
    c: Horizontal(g9)
    c: Coincident(g10,g9)
    c: Vertical(g10)
    c: Coincident(g11,g10)
    c: Coincident(g11,g0)
    c: Horizontal(g11)
    c: Equal(g0,g3)
    c: Equal(g3,g6)
    c: Equal(g6,g9)
    c: Coincident(g6,g7)
    c: Coincident(g9,g8)
    c: Equal(g11,g7)
    c: Equal(g11,g1)
    c: Equal(g2,g4)
    c: Equal(g5,g10)
    c: Coincident(g12,g13)
    c: Coincident(g13,g14)
    c: Coincident(g14,g15)
    c: Coincident(g15,g12)
    c: Horizontal(g13)
    c: Horizontal(g15)
    c: Vertical(g12)
    c: Vertical(g14)
    c: Symmetric(g13,g12,g16)
    c: Coincident(g16,g-1)
    c: Coincident(g13,g1)
    c: Coincident(g7,g12)
    c: DistanceX(g13,g13) = 4
    c: DistanceY(g2,g2) = 10
    c: Equal(g10,g2)
    c: Vertical(g17)
    c: Coincident(g18,g17)
    c: Horizontal(g18)
    c: Coincident(g19,g18)
    c: Vertical(g19)
    c: Coincident(g20,g19)
    c: Horizontal(g20)
    c: Coincident(g21,g20)
    c: Vertical(g21)
    c: Coincident(g22,g21)
    c: Horizontal(g22)
    c: Coincident(g23,g22)
    c: Vertical(g23)
    c: Coincident(g24,g23)
    c: Horizontal(g24)
    c: Coincident(g25,g24)
    c: Vertical(g25)
    c: Coincident(g26,g25)
    c: Horizontal(g26)
    c: Coincident(g27,g26)
    c: Vertical(g27)
    c: Coincident(g28,g27)
    c: Coincident(g28,g17)
    c: Horizontal(g28)
    c: Equal(g26,g18)
    c: Equal(g27,g17)
    c: Equal(g26,g24)
    c: Equal(g20,g24)
    c: Equal(g21,g23)
    c: Equal(g23,g27)
    c: Equal(g22,g25)
    c: DistanceX(g26,g1) = 0.2
    c: DistanceY(g26,g1) = 0.2
    c: DistanceY(g0,g24) = 0.2
    c: Equal(g23,g24)
    c: DistanceX(g16,g25) = 11.55
FEATURE [PartDesign::Pad] Pad011
  Direction = (0,-1,2e-16)
  Length = 2.8
  Length2 = 10
  Placement = pos=(0,0,0) rot=(1,0,0;1.5708rad)
  Profile = -> Sketch020
  ReferenceAxis = -> Sketch020 [N_Axis]
  Type = 0
FEATURE [Sketcher::SketchObject] Sketch021
  FullyConstrained = true
  MapMode = 5
  Placement = pos=(0,0,0) rot=(1,0,0;1.5708rad)
  Support = -> [XZ_Plane012]
  expr: Constraints[53] = Sketch020.Constraints[43]
  expr: Constraints[54] = Sketch020.Constraints[44]
  expr: Constraints[87] = Sketch020.Constraints[77]
  expr: Constraints[88] = Sketch020.Constraints[78]
  expr: Constraints[89] = Sketch020.Constraints[79]
  expr: Constraints[91] = Sketch020.Constraints[81]
  sketch-geometry (34):
    g0: LineSegment StartX=11.55 StartY=11.55 StartZ=0 EndX=11.55 EndY=-11.55 EndZ=0
    g1: LineSegment StartX=11.55 StartY=-11.55 StartZ=0 EndX=-11.55 EndY=-11.55 EndZ=0
    g2: LineSegment StartX=-11.55 StartY=-11.55 StartZ=0 EndX=-11.55 EndY=11.55 EndZ=0
    g3: LineSegment StartX=-11.55 StartY=11.55 StartZ=0 EndX=11.55 EndY=11.55 EndZ=0
    g4: GeomPoint X=0 Y=0 Z=0
    g5: LineSegment StartX=12 StartY=-2 StartZ=0 EndX=12 EndY=2 EndZ=0
    g6: LineSegment StartX=12 StartY=2 StartZ=0 EndX=2 EndY=2 EndZ=0
    g7: LineSegment StartX=2 StartY=2 StartZ=0 EndX=2 EndY=12 EndZ=0
    g8: LineSegment StartX=2 StartY=12 StartZ=0 EndX=-2 EndY=12 EndZ=0
    g9: LineSegment StartX=-2 StartY=12 StartZ=0 EndX=-2 EndY=2 EndZ=0
    g10: LineSegment StartX=-2 StartY=2 StartZ=0 EndX=-12 EndY=2 EndZ=0
    g11: LineSegment StartX=-12 StartY=2 StartZ=0 EndX=-12 EndY=-2 EndZ=0
    g12: LineSegment StartX=-12 StartY=-2 StartZ=0 EndX=-2 EndY=-2 EndZ=0
    g13: LineSegment StartX=-2 StartY=-2 StartZ=0 EndX=-2 EndY=-12 EndZ=0
    g14: LineSegment StartX=-2 StartY=-12 StartZ=0 EndX=2 EndY=-12 EndZ=0
    g15: LineSegment StartX=2 StartY=-12 StartZ=0 EndX=2 EndY=-2 EndZ=0
    g16: LineSegment StartX=2 StartY=-2 StartZ=0 EndX=12 EndY=-2 EndZ=0
    g17: LineSegment StartX=-2 StartY=-2 StartZ=0 EndX=-2 EndY=2 EndZ=0
    g18: LineSegment StartX=-2 StartY=2 StartZ=0 EndX=2 EndY=2 EndZ=0
    g19: LineSegment StartX=2 StartY=2 StartZ=0 EndX=2 EndY=-2 EndZ=0
    g20: LineSegment StartX=2 StartY=-2 StartZ=0 EndX=-2 EndY=-2 EndZ=0
    g21: GeomPoint X=0 Y=0 Z=0
    g22: LineSegment StartX=-1.8 StartY=11.55 StartZ=0 EndX=-1.8 EndY=1.8 EndZ=0
    g23: LineSegment StartX=-1.8 StartY=1.8 StartZ=0 EndX=-11.55 EndY=1.8 EndZ=0
    g24: LineSegment StartX=-11.55 StartY=1.8 StartZ=0 EndX=-11.55 EndY=-1.8 EndZ=0
    g25: LineSegment StartX=-11.55 StartY=-1.8 StartZ=0 EndX=-1.8 EndY=-1.8 EndZ=0
    g26: LineSegment StartX=-1.8 StartY=-1.8 StartZ=0 EndX=-1.8 EndY=-11.55 EndZ=0
    g27: LineSegment StartX=-1.8 StartY=-11.55 StartZ=0 EndX=1.8 EndY=-11.55 EndZ=0
    g28: LineSegment StartX=1.8 StartY=-11.55 StartZ=0 EndX=1.8 EndY=-1.8 EndZ=0
    g29: LineSegment StartX=1.8 StartY=-1.8 StartZ=0 EndX=11.55 EndY=-1.8 EndZ=0
    g30: LineSegment StartX=11.55 StartY=-1.8 StartZ=0 EndX=11.55 EndY=1.8 EndZ=0
    g31: LineSegment StartX=11.55 StartY=1.8 StartZ=0 EndX=1.8 EndY=1.8 EndZ=0
    g32: LineSegment StartX=1.8 StartY=1.8 StartZ=0 EndX=1.8 EndY=11.55 EndZ=0
    g33: LineSegment StartX=1.8 StartY=11.55 StartZ=0 EndX=-1.8 EndY=11.55 EndZ=0
  constraints (94):
    c: Coincident(g0,g1)
    c: Coincident(g1,g2)
    c: Coincident(g2,g3)
    c: Coincident(g3,g0)
    c: Horizontal(g1)
    c: Horizontal(g3)
    c: Vertical(g0)
    c: Vertical(g2)
    c: Symmetric(g1,g0,g4)
    c: Coincident(g4,g-1)
    c: Vertical(g5)
    c: Coincident(g6,g5)
    c: Horizontal(g6)
    c: Coincident(g7,g6)
    c: Vertical(g7)
    c: Coincident(g8,g7)
    c: Horizontal(g8)
    c: Coincident(g9,g8)
    c: Vertical(g9)
    c: Coincident(g10,g9)
    c: Horizontal(g10)
    c: Coincident(g11,g10)
    c: Vertical(g11)
    c: Horizontal(g12)
    c: Coincident(g13,g12)
    c: Vertical(g13)
    c: Horizontal(g14)
    c: Coincident(g15,g14)
    c: Vertical(g15)
    c: Coincident(g16,g15)
    c: Coincident(g16,g5)
    c: Horizontal(g16)
    c: Equal(g5,g8)
    c: Equal(g8,g11)
    c: Equal(g11,g14)
    c: Coincident(g11,g12)
    c: Coincident(g14,g13)
    c: Equal(g16,g12)
    c: Equal(g16,g6)
    c: Equal(g7,g9)
    c: Equal(g10,g15)
    c: Coincident(g17,g18)
    c: Coincident(g18,g19)
    c: Coincident(g19,g20)
    c: Coincident(g20,g17)
    c: Horizontal(g18)
    c: Horizontal(g20)
    c: Vertical(g17)
    c: Vertical(g19)
    c: Symmetric(g18,g17,g21)
    c: Coincident(g21,g-1)
    c: Coincident(g18,g6)
    c: Coincident(g12,g17)
    c: DistanceX(g18,g18) = 4
    c: DistanceY(g7,g7) = 10
    c: Equal(g15,g7)
    c: Vertical(g22)
    c: Coincident(g23,g22)
    c: Horizontal(g23)
    c: Coincident(g24,g23)
    c: Vertical(g24)
    c: Coincident(g25,g24)
    c: Horizontal(g25)
    c: Coincident(g26,g25)
    c: Vertical(g26)
    c: Coincident(g27,g26)
    c: Horizontal(g27)
    c: Coincident(g28,g27)
    c: Vertical(g28)
    c: Coincident(g29,g28)
    c: Horizontal(g29)
    c: Coincident(g30,g29)
    c: Vertical(g30)
    c: Coincident(g31,g30)
    c: Horizontal(g31)
    c: Coincident(g32,g31)
    c: Vertical(g32)
    c: Coincident(g33,g32)
    c: Coincident(g33,g22)
    c: Horizontal(g33)
    c: Equal(g31,g23)
    c: Equal(g32,g22)
    c: Equal(g31,g29)
    c: Equal(g25,g29)
    c: Equal(g26,g28)
    c: Equal(g28,g32)
    c: Equal(g27,g30)
    c: DistanceX(g31,g6) = 0.2
    c: DistanceY(g31,g6) = 0.2
    c: DistanceY(g5,g29) = 0.2
    c: Equal(g28,g29)
    c: DistanceX(g21,g30) = 11.55
    c: PointOnObject(g22,g3)
    c: PointOnObject(g23,g2)
FEATURE [PartDesign::Pad] Pad012
  BaseFeature = -> Pad011
  Direction = (0,-1,2e-16)
  Length = 5
  Length2 = 10
  Placement = pos=(0,0,0) rot=(1,0,0;1.5708rad)
  Profile = -> Sketch021
  ReferenceAxis = -> Sketch021 [N_Axis]
  Reversed = true
  Type = 0
FEATURE [Sketcher::SketchObject] Sketch022
  ExternalGeometry = -> [Cone001]
  FullyConstrained = true
  MapMode = 5
  Placement = pos=(2.3e-15,10.5,-35) rot=(-1,0,0;1.5708rad)
  Support = -> [Cone001]
  expr: Constraints[11] = <<Properties>>.Handle_OD + 2
  sketch-geometry (5):
    g0: LineSegment StartX=-11.75 StartY=-46.75 StartZ=0 EndX=-11.75 EndY=-23.25 EndZ=0
    g1: LineSegment StartX=-11.75 StartY=-23.25 StartZ=0 EndX=11.75 EndY=-23.25 EndZ=0
    g2: LineSegment StartX=11.75 StartY=-23.25 StartZ=0 EndX=11.75 EndY=-46.75 EndZ=0
    g3: LineSegment StartX=11.75 StartY=-46.75 StartZ=0 EndX=-11.75 EndY=-46.75 EndZ=0
    g4: GeomPoint X=-2.3e-15 Y=-35 Z=0
  constraints (12):
    c: Coincident(g0,g1)
    c: Coincident(g1,g2)
    c: Coincident(g2,g3)
    c: Coincident(g3,g0)
    c: Horizontal(g1)
    c: Horizontal(g3)
    c: Vertical(g0)
    c: Vertical(g2)
    c: Symmetric(g1,g0,g4)
    c: Coincident(g4,g-3)
    c: Equal(g2,g1)
    c: DistanceX(g1,g1) = 23.5
FEATURE [PartDesign::Pocket] Pocket010
  BaseFeature = -> Cone001
  Direction = (-2e-16,-1,2e-16)
  Length = 8
  Length2 = 5
  Placement = pos=(0,0,-35) rot=(1,0,0;3.14159rad)
  Profile = -> Sketch022
  ReferenceAxis = -> Sketch022 [N_Axis]
  Type = 0
FEATURE [Sketcher::SketchObject] Sketch023
  FullyConstrained = true
  MapMode = 5
  Placement = pos=(0,5,-2.2e-15) rot=(-1,0,0;1.5708rad)
  Support = -> [Pad012]
  sketch-geometry (1):
    g0: Circle CenterX=0 CenterY=0 CenterZ=0 NormalX=0 NormalY=0 NormalZ=1 AngleXU=0 Radius=2.5
  constraints (2):
    c: Coincident(g0,g-1)
    c: Diameter(g0) = 5
FEATURE [PartDesign::Pad] Pad013
  BaseFeature = -> Pad012
  Direction = (0,1,-2e-16)
  Length = 3
  Length2 = 10
  Placement = pos=(0,0,0) rot=(1,0,0;1.5708rad)
  Profile = -> Sketch023
  ReferenceAxis = -> Sketch023 [N_Axis]
  Type = 0
FEATURE [PartDesign::Fillet] Fillet
  Base = -> Pad013 [Edge51]
  BaseFeature = -> Pad013
  Placement = pos=(0,0,0) rot=(1,0,0;1.5708rad)
  Radius = 2
  SupportTransform = false
  UseAllEdges = false
FEATURE [Sketcher::SketchObject] Sketch024
  ExternalGeometry = -> [Cone001]
  FullyConstrained = true
  MapMode = 5
  Placement = pos=(6e-16,2.5,-35) rot=(-1,0,0;1.5708rad)
  Support = -> [Pocket010]
  expr: Constraints[11] = Sketch022.Constraints[11]
  expr: Constraints[54] = Sketch019.Constraints[43]
  expr: Constraints[55] = Sketch019.Constraints[44]
  sketch-geometry (34):
    g0: LineSegment StartX=-11.75 StartY=-46.75 StartZ=0 EndX=-11.75 EndY=-23.25 EndZ=0
    g1: LineSegment StartX=-11.75 StartY=-23.25 StartZ=0 EndX=11.75 EndY=-23.25 EndZ=0
    g2: LineSegment StartX=11.75 StartY=-23.25 StartZ=0 EndX=11.75 EndY=-46.75 EndZ=0
    g3: LineSegment StartX=11.75 StartY=-46.75 StartZ=0 EndX=-11.75 EndY=-46.75 EndZ=0
    g4: GeomPoint X=-2.4e-15 Y=-35 Z=0
    g5: LineSegment StartX=12 StartY=-37 StartZ=0 EndX=12 EndY=-33 EndZ=0
    g6: LineSegment StartX=12 StartY=-33 StartZ=0 EndX=2 EndY=-33 EndZ=0
    g7: LineSegment StartX=2 StartY=-33 StartZ=0 EndX=2 EndY=-23 EndZ=0
    g8: LineSegment StartX=2 StartY=-23 StartZ=0 EndX=-2 EndY=-23 EndZ=0
    g9: LineSegment StartX=-2 StartY=-23 StartZ=0 EndX=-2 EndY=-33 EndZ=0
    g10: LineSegment StartX=-2 StartY=-33 StartZ=0 EndX=-12 EndY=-33 EndZ=0
    g11: LineSegment StartX=-12 StartY=-33 StartZ=0 EndX=-12 EndY=-37 EndZ=0
    g12: LineSegment StartX=-12 StartY=-37 StartZ=0 EndX=-2 EndY=-37 EndZ=0
    g13: LineSegment StartX=-2 StartY=-37 StartZ=0 EndX=-2 EndY=-47 EndZ=0
    g14: LineSegment StartX=-2 StartY=-47 StartZ=0 EndX=2 EndY=-47 EndZ=0
    g15: LineSegment StartX=2 StartY=-47 StartZ=0 EndX=2 EndY=-37 EndZ=0
    g16: LineSegment StartX=2 StartY=-37 StartZ=0 EndX=12 EndY=-37 EndZ=0
    g17: LineSegment StartX=-2 StartY=-37 StartZ=0 EndX=-2 EndY=-33 EndZ=0
    g18: LineSegment StartX=-2 StartY=-33 StartZ=0 EndX=2 EndY=-33 EndZ=0
    g19: LineSegment StartX=2 StartY=-33 StartZ=0 EndX=2 EndY=-37 EndZ=0
    g20: LineSegment StartX=2 StartY=-37 StartZ=0 EndX=-2 EndY=-37 EndZ=0
    g21: GeomPoint X=0 Y=0 Z=0
    g22: LineSegment StartX=-2 StartY=-23.25 StartZ=0 EndX=2 EndY=-23.25 EndZ=0
    g23: LineSegment StartX=2 StartY=-23.25 StartZ=0 EndX=2 EndY=-33 EndZ=0
    g24: LineSegment StartX=2 StartY=-33 StartZ=0 EndX=11.75 EndY=-33 EndZ=0
    g25: LineSegment StartX=11.75 StartY=-33 StartZ=0 EndX=11.75 EndY=-37 EndZ=0
    g26: LineSegment StartX=11.75 StartY=-37 StartZ=0 EndX=2 EndY=-37 EndZ=0
    g27: LineSegment StartX=2 StartY=-37 StartZ=0 EndX=2 EndY=-46.75 EndZ=0
    g28: LineSegment StartX=2 StartY=-46.75 StartZ=0 EndX=-2 EndY=-46.75 EndZ=0
    g29: LineSegment StartX=-2 StartY=-46.75 StartZ=0 EndX=-2 EndY=-37 EndZ=0
    g30: LineSegment StartX=-2 StartY=-37 StartZ=0 EndX=-11.75 EndY=-37 EndZ=0
    g31: LineSegment StartX=-11.75 StartY=-37 StartZ=0 EndX=-11.75 EndY=-33 EndZ=0
    g32: LineSegment StartX=-11.75 StartY=-33 StartZ=0 EndX=-2 EndY=-33 EndZ=0
    g33: LineSegment StartX=-2 StartY=-33 StartZ=0 EndX=-2 EndY=-23.25 EndZ=0
  constraints (90):
    c: Coincident(g0,g1)
    c: Coincident(g1,g2)
    c: Coincident(g2,g3)
    c: Coincident(g3,g0)
    c: Horizontal(g1)
    c: Horizontal(g3)
    c: Vertical(g0)
    c: Vertical(g2)
    c: Symmetric(g1,g0,g4)
    c: Coincident(g4,g-3)
    c: Equal(g2,g1)
    c: DistanceX(g1,g1) = 23.5
    c: Vertical(g5)
    c: Coincident(g6,g5)
    c: Horizontal(g6)
    c: Coincident(g7,g6)
    c: Vertical(g7)
    c: Coincident(g8,g7)
    c: Horizontal(g8)
    c: Coincident(g9,g8)
    c: Vertical(g9)
    c: Coincident(g10,g9)
    c: Horizontal(g10)
    c: Coincident(g11,g10)
    c: Vertical(g11)
    c: Horizontal(g12)
    c: Coincident(g13,g12)
    c: Vertical(g13)
    c: Horizontal(g14)
    c: Coincident(g15,g14)
    c: Vertical(g15)
    c: Coincident(g16,g15)
    c: Coincident(g16,g5)
    c: Horizontal(g16)
    c: Equal(g5,g8)
    c: Equal(g8,g11)
    c: Equal(g11,g14)
    c: Coincident(g11,g12)
    c: Coincident(g14,g13)
    c: Equal(g16,g12)
    c: Equal(g16,g6)
    c: Equal(g7,g9)
    c: Equal(g10,g15)
    c: Coincident(g17,g18)
    c: Coincident(g18,g19)
    c: Coincident(g19,g20)
    c: Coincident(g20,g17)
    c: Horizontal(g18)
    c: Horizontal(g20)
    c: Vertical(g17)
    c: Vertical(g19)
    c: Coincident(g21,g-1)
    c: Coincident(g18,g6)
    c: Coincident(g12,g17)
    c: DistanceX(g18,g18) = 4
    c: DistanceY(g7,g7) = 10
    c: Equal(g15,g7)
    c: Symmetric(g6,g12,g4)
    c: PointOnObject(g22,g9)
    c: PointOnObject(g22,g1)
    c: Horizontal(g22)
    c: PointOnObject(g22,g7)
    c: Coincident(g23,g22)
    c: Coincident(g23,g6)
    c: Coincident(g24,g23)
    c: PointOnObject(g24,g2)
    c: Horizontal(g24)
    c: Coincident(g25,g24)
    c: PointOnObject(g25,g16)
    c: Vertical(g25)
    c: Coincident(g26,g25)
    c: Coincident(g26,g15)
    c: Coincident(g27,g26)
    c: PointOnObject(g27,g3)
    c: Vertical(g27)
    c: Coincident(g28,g27)
    c: PointOnObject(g28,g13)
    c: Horizontal(g28)
    c: Coincident(g29,g28)
    c: Coincident(g29,g12)
    c: Coincident(g30,g29)
    c: PointOnObject(g30,g0)
    c: Horizontal(g30)
    c: Coincident(g31,g30)
    c: PointOnObject(g31,g10)
    c: Vertical(g31)
    c: Coincident(g32,g31)
    c: Coincident(g32,g9)
    c: Coincident(g33,g32)
    c: Coincident(g33,g22)
FEATURE [PartDesign::Pocket] Pocket011
  BaseFeature = -> Pocket010
  Direction = (-2e-16,-1,2e-16)
  Length = 3
  Length2 = 5
  Placement = pos=(0,0,-35) rot=(1,0,0;3.14159rad)
  Profile = -> Sketch024
  ReferenceAxis = -> Sketch024 [N_Axis]
  Type = 0
FEATURE [PartDesign::Body] Body  label="HeadInstert"
  Group = -> [Sketch,Pad,Sketch001,Pocket,Sketch002,Pocket001,Sketch004,Pocket002,Chamfer,Sketch003,Pocket003,Chamfer001,Sketch008,Pocket006,Chamfer003,Chamfer004,Chamfer005,Cone,Cone001,Sketch022,Pocket010,Sketch024,Pocket011]
  Origin = -> Origin001
  Tip = -> Pocket011
FEATURE [PartDesign::Fillet] Fillet001
  Base = -> Fillet [Edge3]
  BaseFeature = -> Fillet
  Placement = pos=(0,0,0) rot=(1,0,0;1.5708rad)
  Radius = 7
  SupportTransform = false
  UseAllEdges = false
FEATURE [Sketcher::SketchObject] Sketch025
  FullyConstrained = true
  MapMode = 5
  Placement = pos=(0,0,0) rot=(1,0,0;1.5708rad)
  Support = -> [XZ_Plane012]
  expr: Constraints[1] = <<Properties>>.Handle_OD - <<Properties>>.Clearance * 2
  sketch-geometry (1):
    g0: Circle CenterX=0 CenterY=0 CenterZ=0 NormalX=0 NormalY=0 NormalZ=1 AngleXU=0 Radius=10.55
  constraints (2):
    c: Coincident(g0,g-1)
    c: Diameter(g0) = 21.1
FEATURE [PartDesign::Pad] Pad014
  BaseFeature = -> Fillet001
  Direction = (0,-1,2e-16)
  Length = 9
  Length2 = 10
  Placement = pos=(0,0,0) rot=(1,0,0;1.5708rad)
  Profile = -> Sketch025
  ReferenceAxis = -> Sketch025 [N_Axis]
  TaperAngle = -2
  Type = 0
FEATURE [PartDesign::Chamfer] Chamfer006
  Angle = 45
  Base = -> Pad014 [Edge15,Edge19,Edge10,Edge11]
  BaseFeature = -> Pad014
  ChamferType = 0
  FlipDirection = false
  Placement = pos=(0,0,0) rot=(1,0,0;1.5708rad)
  Size = 1
  Size2 = 1
  SupportTransform = false
  UseAllEdges = false
FEATURE [PartDesign::Body] Body012  label="Pusher"
  Group = -> [Sketch020,Pad011,Sketch021,Pad012,Sketch023,Pad013,Fillet,Fillet001,Sketch025,Pad014,Chamfer006]
  Origin = -> Origin012
  Placement = pos=(0,2.5,0) rot=(0,0,1;0rad)
  Tip = -> Chamfer006
FEATURE [Sketcher::SketchObject] Sketch026
  FullyConstrained = true
  MapMode = 5
  Placement = pos=(0,0,0) rot=(1,0,0;1.5708rad)
  Support = -> [XZ_Plane013]
  expr: Constraints[1] = <<Properties>>.Handle_OD - 1
  sketch-geometry (2):
    g0: Circle CenterX=0 CenterY=0 CenterZ=0 NormalX=0 NormalY=0 NormalZ=1 AngleXU=0 Radius=10.25
    g1: Circle CenterX=0 CenterY=0 CenterZ=0 NormalX=0 NormalY=0 NormalZ=1 AngleXU=0 Radius=4
  constraints (4):
    c: Coincident(g0,g-1)
    c: Diameter(g0) = 20.5
    c: Coincident(g1,g0)
    c: Diameter(g1) = 8
FEATURE [PartDesign::Pad] Pad015
  Direction = (0,-1,-2e-16)
  Length = 10
  Length2 = 10
  Placement = pos=(0,0,0) rot=(1,0,0;1.5708rad)
  Profile = -> Sketch026
  ReferenceAxis = -> Sketch026 [N_Axis]
  Type = 0
FEATURE [TechDraw::DrawSVGTemplate] Template
  EditableTexts = AuthorName=Alex Anastasakis; CheckDate=2024/11/11; CreationDate=2024/11/9; DrawingNumber=7; FC-Scale=1:1; FC-Title=Head Inner; SheetNumber=1 of 1; Subtitle=Course: Industrial Design for Game Hardware; SupervisorName=Alvaro Uribe Quevedo; Weight=0.055
  Height = 297
  Orientation = 1
  Template = C:/Program Files/FreeCAD 0.21/data/Mod/TechDraw/Templates/A3_LandscapeTD.svg
  Width = 420
FEATURE [TechDraw::DrawProjGroupItem] ProjItem  label="Front"
  Caption = See section A
  CoarseView = false
  Direction = (0,0,1)
  Focus = 100
  HardHidden = false
  IsoCount = 0
  IsoHidden = false
  IsoVisible = false
  LockPosition = true
  Perspective = false
  Rotation = 0
  RotationVector = (1,0,0)
  ScaleType = 2
  ScrubCount = 0
  SeamHidden = false
  SeamVisible = false
  SmoothHidden = false
  SmoothVisible = true
  Source = -> [Body]
  Type = 0
  X = 0
  XDirection = (1,0,0)
  Y = 0
FEATURE [TechDraw::DrawProjGroupItem] ProjItem004  label="Iso"
  CoarseView = false
  Direction = (0.57735,0.57735,0.57735)
  Focus = 100
  HardHidden = false
  IsoCount = 0
  IsoHidden = false
  IsoVisible = false
  LockPosition = false
  Perspective = false
  Rotation = 0
  RotationVector = (1,0,0)
  ScaleType = 2
  ScrubCount = 0
  SeamHidden = false
  SeamVisible = false
  SmoothHidden = false
  SmoothVisible = true
  Source = -> [Body]
  Type = 7
  X = 108.621
  XDirection = (0.707107,0,-0.707107)
  Y = 93.2929
FEATURE [TechDraw::DrawViewDimension] Dimension002
  AngleOverride = false
  Arbitrary = false
  ArbitraryTolerances = false
  EqualTolerance = true
  ExtensionAngle = 0
  FormatSpec = %.2w
  FormatSpecOverTolerance = %+.2w
  FormatSpecUnderTolerance = %+.2w
  Inverted = false
  LineAngle = 0
  LockPosition = false
  MeasureType = 1
  OverTolerance = 0
  References2D = -> [ProjItem]
  Rotation = 0
  ScaleType = 0
  TheoreticalExact = false
  Type = 1
  UnderTolerance = 0
  X = 13.4101
  Y = -26.9391
FEATURE [TechDraw::DrawProjGroupItem] ProjItem001  label="Top"
  CoarseView = false
  Direction = (0,1,0)
  Focus = 100
  HardHidden = false
  IsoCount = 0
  IsoHidden = false
  IsoVisible = false
  LockPosition = false
  Perspective = false
  Rotation = 0
  RotationVector = (1,0,0)
  ScaleType = 2
  ScrubCount = 0
  SeamHidden = false
  SeamVisible = false
  SmoothHidden = false
  SmoothVisible = true
  Source = -> [Body]
  Type = 4
  X = 0
  XDirection = (1,0,0)
  Y = 93.2929
FEATURE [TechDraw::DrawViewDimension] Dimension014
  AngleOverride = false
  Arbitrary = false
  ArbitraryTolerances = false
  EqualTolerance = true
  ExtensionAngle = 0
  FormatSpec = %.2w
  FormatSpecOverTolerance = %+.2w
  FormatSpecUnderTolerance = %+.2w
  Inverted = false
  LineAngle = 0
  LockPosition = false
  MeasureType = 1
  OverTolerance = 0
  References2D = -> [ProjItem001]
  Rotation = 0
  ScaleType = 0
  TheoreticalExact = false
  Type = 2
  UnderTolerance = 0
  X = -38.5007
  Y = -0.941511
FEATURE [TechDraw::DrawViewDimension] Dimension012
  AngleOverride = false
  Arbitrary = false
  ArbitraryTolerances = false
  EqualTolerance = true
  ExtensionAngle = 0
  FormatSpec = %.2w
  FormatSpecOverTolerance = %+.2w
  FormatSpecUnderTolerance = %+.2w
  Inverted = false
  LineAngle = 0
  LockPosition = false
  MeasureType = 1
  OverTolerance = 0
  References2D = -> [ProjItem001]
  Rotation = 0
  ScaleType = 0
  TheoreticalExact = false
  Type = 2
  UnderTolerance = 0
  X = -31.524
  Y = 5.3649
FEATURE [TechDraw::DrawViewSection] SectionView  label="Section A"
  BaseView = -> ProjItem
  Caption = Scale 1:1
  CoarseView = false
  CutSurfaceDisplay = 2
  Direction = (-1,-1e-16,0)
  FileGeomPattern = C:/Program Files/FreeCAD 0.21/data/Mod/TechDraw/PAT/FCPAT.pat
  FileHatchPattern = C:/Program Files/FreeCAD 0.21/data/Mod/TechDraw/Patterns/simple.svg
  Focus = 100
  FuseBeforeCut = false
  HardHidden = false
  HatchOffset = (0,0,0)
  HatchRotation = 0
  HatchScale = 1
  IsoCount = 0
  IsoHidden = false
  IsoVisible = false
  LockPosition = false
  NameGeomPattern = Diamond
  Perspective = false
  Rotation = -90
  ScaleType = 2
  ScrubCount = 0
  SeamHidden = false
  SeamVisible = false
  SectionDirection = 4
  SectionNormal = (-1,-1e-16,0)
  SectionOrigin = (0,0.16,0)
  SmoothHidden = false
  SmoothVisible = true
  Source = -> [Body]
  TrimAfterCut = false
  X = 92.412
  XDirection = (1e-16,-1,0)
  Y = 135.414
FEATURE [TechDraw::DrawProjGroupItem] ProjItem005  label="Right"
  Caption = See section B
  CoarseView = false
  Direction = (1,0,1e-16)
  Focus = 100
  HardHidden = false
  IsoCount = 0
  IsoHidden = false
  IsoVisible = false
  LockPosition = false
  Perspective = false
  Rotation = 0
  RotationVector = (1,0,0)
  ScaleType = 2
  ScrubCount = 0
  SeamHidden = false
  SeamVisible = false
  SmoothHidden = false
  SmoothVisible = true
  Source = -> [Body]
  Type = 2
  X = 108.621
  XDirection = (1e-16,0,-1)
  Y = 0
FEATURE [TechDraw::DrawProjGroup] ProjGroup
  Anchor = -> ProjItem
  AutoDistribute = true
  LockPosition = false
  ProjectionType = 1
  Rotation = 0
  ScaleType = 0
  Source = -> [Body]
  Views = -> [ProjItem,ProjItem001,ProjItem004,ProjItem005]
  X = 204.726
  Y = 140.758
  spacingX = 40
  spacingY = 30
FEATURE [TechDraw::DrawViewSection] SectionView001  label="Section B"
  BaseView = -> ProjItem005
  Caption = Scale 1:1
  CoarseView = false
  CutSurfaceDisplay = 2
  Direction = (-1e-16,-1e-16,1)
  FileGeomPattern = C:/Program Files/FreeCAD 0.21/data/Mod/TechDraw/PAT/FCPAT.pat
  FileHatchPattern = C:/Program Files/FreeCAD 0.21/data/Mod/TechDraw/Patterns/simple.svg
  Focus = 100
  FuseBeforeCut = false
  HardHidden = false
  HatchOffset = (0,0,0)
  HatchRotation = 0
  HatchScale = 1
  IsoCount = 0
  IsoHidden = false
  IsoVisible = false
  LockPosition = false
  NameGeomPattern = Diamond
  Perspective = false
  Rotation = -90
  ScaleType = 2
  ScrubCount = 0
  SeamHidden = false
  SeamVisible = false
  SectionDirection = 4
  SectionNormal = (-1e-16,-1e-16,1)
  SectionOrigin = (0,0.16,0)
  SmoothHidden = false
  SmoothVisible = true
  Source = -> [Body]
  TrimAfterCut = false
  X = 79.5769
  XDirection = (0,-1,-1e-16)
  Y = 239.74
FEATURE [TechDraw::DrawViewDimension] Dimension017
  AngleOverride = false
  Arbitrary = false
  ArbitraryTolerances = false
  EqualTolerance = true
  ExtensionAngle = 0
  FormatSpec = %.0w
  FormatSpecOverTolerance = %+.2w
  FormatSpecUnderTolerance = %+.2w
  Inverted = false
  LineAngle = 0
  LockPosition = false
  MeasureType = 1
  OverTolerance = 0
  References2D = -> [SectionView]
  Rotation = 0
  ScaleType = 0
  TheoreticalExact = false
  Type = 2
  UnderTolerance = 0
  X = -50.5027
  Y = -4.81952
FEATURE [TechDraw::DrawViewDimension] Dimension021
  AngleOverride = false
  Arbitrary = false
  ArbitraryTolerances = false
  EqualTolerance = true
  ExtensionAngle = 0
  FormatSpec = %.0w x35°
  FormatSpecOverTolerance = %+.2w
  FormatSpecUnderTolerance = %+.2w
  Inverted = false
  LineAngle = 0
  LockPosition = false
  MeasureType = 1
  OverTolerance = 0
  References2D = -> [SectionView]
  Rotation = 0
  ScaleType = 0
  TheoreticalExact = false
  Type = 1
  UnderTolerance = 0
  X = -28.3778
  Y = -35.6055
FEATURE [TechDraw::DrawViewDimension] Dimension022
  AngleOverride = false
  Arbitrary = false
  ArbitraryTolerances = false
  EqualTolerance = true
  ExtensionAngle = 0
  FormatSpec = %.0w x55°
  FormatSpecOverTolerance = %+.2w
  FormatSpecUnderTolerance = %+.2w
  Inverted = false
  LineAngle = 0
  LockPosition = false
  MeasureType = 1
  OverTolerance = 0
  References2D = -> [SectionView]
  Rotation = 0
  ScaleType = 0
  TheoreticalExact = false
  Type = 1
  UnderTolerance = 0
  X = -46.7088
  Y = -28.8852
FEATURE [TechDraw::DrawViewDimension] Dimension023
  AngleOverride = false
  Arbitrary = false
  ArbitraryTolerances = false
  EqualTolerance = true
  ExtensionAngle = 0
  FormatSpec = %.2w
  FormatSpecOverTolerance = %+.2w
  FormatSpecUnderTolerance = %+.2w
  Inverted = false
  LineAngle = 0
  LockPosition = false
  MeasureType = 1
  OverTolerance = 0
  References2D = -> [SectionView001]
  Rotation = 0
  ScaleType = 0
  TheoreticalExact = false
  Type = 2
  UnderTolerance = 0
  X = 35.071
  Y = 21.2076
FEATURE [TechDraw::DrawViewDimension] Dimension024
  AngleOverride = false
  Arbitrary = false
  ArbitraryTolerances = false
  EqualTolerance = true
  ExtensionAngle = 0
  FormatSpec = %.2w x35°
  FormatSpecOverTolerance = %+.2w
  FormatSpecUnderTolerance = %+.2w
  Inverted = false
  LineAngle = 0
  LockPosition = false
  MeasureType = 1
  OverTolerance = 0
  References2D = -> [SectionView001]
  Rotation = 0
  ScaleType = 0
  TheoreticalExact = false
  Type = 1
  UnderTolerance = 0
  X = 35.3183
  Y = 31.104
FEATURE [TechDraw::DrawViewDimension] Dimension029
  AngleOverride = false
  Arbitrary = false
  ArbitraryTolerances = false
  EqualTolerance = true
  ExtensionAngle = 0
  FormatSpec = %.2w
  FormatSpecOverTolerance = %+.2w
  FormatSpecUnderTolerance = %+.2w
  Inverted = false
  LineAngle = 0
  LockPosition = false
  MeasureType = 1
  OverTolerance = 0
  References2D = -> [SectionView]
  Rotation = 0
  ScaleType = 0
  TheoreticalExact = false
  Type = 2
  UnderTolerance = 0
  X = -43.1914
  Y = 3.41903
FEATURE [TechDraw::DrawViewDimension] Dimension030
  AngleOverride = false
  Arbitrary = false
  ArbitraryTolerances = false
  EqualTolerance = true
  ExtensionAngle = 0
  FormatSpec = ⌀%.2w
  FormatSpecOverTolerance = %+.2w
  FormatSpecUnderTolerance = %+.2w
  Inverted = false
  LineAngle = 0
  LockPosition = false
  MeasureType = 1
  OverTolerance = 0
  References2D = -> [ProjItem]
  Rotation = 0
  ScaleType = 0
  TheoreticalExact = false
  Type = 5
  UnderTolerance = 0
  X = 30.1886
  Y = 21.1788
FEATURE [TechDraw::DrawViewDimension] Dimension031
  AngleOverride = false
  Arbitrary = false
  ArbitraryTolerances = false
  EqualTolerance = true
  ExtensionAngle = 0
  FormatSpec = ⌀%.2w
  FormatSpecOverTolerance = %+.2w
  FormatSpecUnderTolerance = %+.2w
  Inverted = false
  LineAngle = 0
  LockPosition = false
  MeasureType = 1
  OverTolerance = 0
  References2D = -> [ProjItem]
  Rotation = 0
  ScaleType = 0
  TheoreticalExact = false
  Type = 5
  UnderTolerance = 0
  X = -29.9546
  Y = 17.6685
FEATURE [TechDraw::DrawViewDimension] Dimension032
  AngleOverride = false
  Arbitrary = false
  ArbitraryTolerances = false
  EqualTolerance = true
  ExtensionAngle = 0
  FormatSpec = ⌀%.2w
  FormatSpecOverTolerance = %+.2w
  FormatSpecUnderTolerance = %+.2w
  Inverted = false
  LineAngle = 0
  LockPosition = false
  MeasureType = 1
  OverTolerance = 0
  References2D = -> [ProjItem]
  Rotation = 0
  ScaleType = 0
  TheoreticalExact = false
  Type = 5
  UnderTolerance = 0
  X = 33.6989
  Y = -21.8809
FEATURE [TechDraw::DrawViewDimension] Dimension033
  AngleOverride = false
  Arbitrary = false
  ArbitraryTolerances = false
  EqualTolerance = true
  ExtensionAngle = 0
  FormatSpec = %.2w
  FormatSpecOverTolerance = %+.2w
  FormatSpecUnderTolerance = %+.2w
  Inverted = false
  LineAngle = 0
  LockPosition = false
  MeasureType = 1
  OverTolerance = 0
  References2D = -> [ProjItem001]
  Rotation = 0
  ScaleType = 0
  TheoreticalExact = false
  Type = 2
  UnderTolerance = 0
  X = -32.2736
  Y = 28.3195
FEATURE [TechDraw::DrawViewDimension] Dimension034
  AngleOverride = false
  Arbitrary = false
  ArbitraryTolerances = false
  EqualTolerance = true
  ExtensionAngle = 0
  FormatSpec = %.2w
  FormatSpecOverTolerance = %+.2w
  FormatSpecUnderTolerance = %+.2w
  Inverted = false
  LineAngle = 0
  LockPosition = false
  MeasureType = 1
  OverTolerance = 0
  References2D = -> [ProjItem001]
  Rotation = 0
  ScaleType = 0
  TheoreticalExact = false
  Type = 2
  UnderTolerance = 0
  X = -52.4798
  Y = -1.28726
FEATURE [TechDraw::DrawViewDimension] Dimension035
  AngleOverride = false
  Arbitrary = false
  ArbitraryTolerances = false
  EqualTolerance = true
  ExtensionAngle = 0
  FormatSpec = %.2w
  FormatSpecOverTolerance = %+.2w
  FormatSpecUnderTolerance = %+.2w
  Inverted = false
  LineAngle = 0
  LockPosition = false
  MeasureType = 1
  OverTolerance = 0
  References2D = -> [SectionView001]
  Rotation = 0
  ScaleType = 0
  TheoreticalExact = false
  Type = 2
  UnderTolerance = 0
  X = 30.3114
  Y = -7.19245
FEATURE [TechDraw::DrawViewDimension] Dimension036
  AngleOverride = false
  Arbitrary = false
  ArbitraryTolerances = false
  EqualTolerance = true
  ExtensionAngle = 0
  FormatSpec = %.2w
  FormatSpecOverTolerance = %+.2w
  FormatSpecUnderTolerance = %+.2w
  Inverted = false
  LineAngle = 0
  LockPosition = false
  MeasureType = 1
  OverTolerance = 0
  References2D = -> [SectionView001]
  Rotation = 0
  ScaleType = 0
  TheoreticalExact = false
  Type = 2
  UnderTolerance = 0
  X = -31.8399
  Y = -3.84414
FEATURE [TechDraw::DrawViewDimension] Dimension037
  AngleOverride = false
  Arbitrary = false
  ArbitraryTolerances = false
  EqualTolerance = true
  ExtensionAngle = 0
  FormatSpec = %.2w
  FormatSpecOverTolerance = %+.2w
  FormatSpecUnderTolerance = %+.2w
  Inverted = false
  LineAngle = 0
  LockPosition = false
  MeasureType = 1
  OverTolerance = 0
  References2D = -> [SectionView001]
  Rotation = 0
  ScaleType = 0
  TheoreticalExact = false
  Type = 1
  UnderTolerance = 0
  X = 11.6916
  Y = -25.7266
FEATURE [TechDraw::DrawViewDimension] Dimension038
  AngleOverride = false
  Arbitrary = false
  ArbitraryTolerances = false
  EqualTolerance = true
  ExtensionAngle = 0
  FormatSpec = %.2w x45°
  FormatSpecOverTolerance = %+.2w
  FormatSpecUnderTolerance = %+.2w
  Inverted = false
  LineAngle = 0
  LockPosition = false
  MeasureType = 1
  OverTolerance = 0
  References2D = -> [SectionView]
  Rotation = 0
  ScaleType = 0
  TheoreticalExact = false
  Type = 1
  UnderTolerance = 0
  X = 31.3138
  Y = 36.1028
FEATURE [TechDraw::DrawViewDimension] Dimension
  AngleOverride = false
  Arbitrary = false
  ArbitraryTolerances = false
  EqualTolerance = true
  ExtensionAngle = 0
  FormatSpec = ⌀%.2w
  FormatSpecOverTolerance = %+.2w
  FormatSpecUnderTolerance = %+.2w
  Inverted = false
  LineAngle = 0
  LockPosition = false
  MeasureType = 1
  OverTolerance = 0
  References2D = -> [ProjItem001]
  Rotation = 0
  ScaleType = 0
  TheoreticalExact = false
  Type = 5
  UnderTolerance = 0
  X = 38.909
  Y = 16.8636
FEATURE [TechDraw::DrawViewDimension] Dimension040
  AngleOverride = false
  Arbitrary = false
  ArbitraryTolerances = false
  EqualTolerance = true
  ExtensionAngle = 0
  FormatSpec = %.0w
  FormatSpecOverTolerance = %+.2w
  FormatSpecUnderTolerance = %+.2w
  Inverted = false
  LineAngle = 0
  LockPosition = false
  MeasureType = 1
  OverTolerance = 0
  References2D = -> [SectionView]
  Rotation = 0
  ScaleType = 0
  TheoreticalExact = false
  Type = 2
  UnderTolerance = 0
  X = 39.5876
  Y = -32.4773
FEATURE [TechDraw::DrawViewDimension] Dimension041
  AngleOverride = false
  Arbitrary = false
  ArbitraryTolerances = false
  EqualTolerance = true
  ExtensionAngle = 0
  FormatSpec = %.0w
  FormatSpecOverTolerance = %+.2w
  FormatSpecUnderTolerance = %+.2w
  Inverted = false
  LineAngle = 0
  LockPosition = false
  MeasureType = 1
  OverTolerance = 0
  References2D = -> [SectionView]
  Rotation = 0
  ScaleType = 0
  TheoreticalExact = false
  Type = 2
  UnderTolerance = 0
  X = 51.5623
  Y = -13.4641
FEATURE [TechDraw::DrawViewDimension] Dimension042
  AngleOverride = false
  Arbitrary = false
  ArbitraryTolerances = false
  EqualTolerance = true
  ExtensionAngle = 0
  FormatSpec = %.2w
  FormatSpecOverTolerance = %+.2w
  FormatSpecUnderTolerance = %+.2w
  Inverted = false
  LineAngle = 0
  LockPosition = false
  MeasureType = 1
  OverTolerance = 0
  References2D = -> [ProjItem001]
  Rotation = 0
  ScaleType = 0
  TheoreticalExact = false
  Type = 1
  UnderTolerance = 0
  X = -5.91587
  Y = 48.6076
FEATURE [TechDraw::DrawViewDimension] Dimension043
  AngleOverride = false
  Arbitrary = false
  ArbitraryTolerances = false
  EqualTolerance = true
  ExtensionAngle = 0
  FormatSpec = %.2w
  FormatSpecOverTolerance = %+.2w
  FormatSpecUnderTolerance = %+.2w
  Inverted = false
  LineAngle = 0
  LockPosition = false
  MeasureType = 1
  OverTolerance = 0
  References2D = -> [ProjItem001]
  Rotation = 0
  ScaleType = 0
  TheoreticalExact = false
  Type = 2
  UnderTolerance = 0
  X = -45.4794
  Y = 5.06898
FEATURE [TechDraw::DrawViewDimension] Dimension044
  AngleOverride = false
  Arbitrary = false
  ArbitraryTolerances = false
  EqualTolerance = true
  ExtensionAngle = 0
  FormatSpec = %.2w
  FormatSpecOverTolerance = %+.2w
  FormatSpecUnderTolerance = %+.2w
  Inverted = false
  LineAngle = 0
  LockPosition = false
  MeasureType = 1
  OverTolerance = 0
  References2D = -> [ProjItem001]
  Rotation = 0
  ScaleType = 0
  TheoreticalExact = false
  Type = 1
  UnderTolerance = 0
  X = 1.58855
  Y = 43.6726
FEATURE [TechDraw::DrawSVGTemplate] Template001
  EditableTexts = AuthorName=Alex Anastasakis; CheckDate=2024/11/11; CreationDate=2024/11/10; DrawingNumber=3; FC-Scale=2:1; FC-Title=Head Top Cover; SheetNumber=1 of 1; Subtitle=Course: Industrial Design for Game Hardware; SupervisorName=Alvaro Uribe Quevedo; Weight=0.007
  Height = 297
  Orientation = 1
  Template = C:/Program Files/FreeCAD 0.21/data/Mod/TechDraw/Templates/A3_LandscapeTD.svg
  Width = 420
FEATURE [TechDraw::DrawProjGroupItem] ProjItem006  label="Front001"
  CoarseView = false
  Direction = (0,0,1)
  Focus = 100
  HardHidden = false
  IsoCount = 0
  IsoHidden = false
  IsoVisible = false
  LockPosition = true
  Perspective = false
  Rotation = 0
  RotationVector = (1,0,0)
  Scale = 2
  ScaleType = 2
  ScrubCount = 0
  SeamHidden = false
  SeamVisible = false
  SmoothHidden = false
  SmoothVisible = true
  Source = -> [Body001]
  Type = 0
  X = 0
  XDirection = (1,0,0)
  Y = 0
FEATURE [TechDraw::DrawProjGroupItem] ProjItem007  label="Bottom"
  CoarseView = false
  Direction = (0,-1,0)
  Focus = 100
  HardHidden = false
  IsoCount = 0
  IsoHidden = false
  IsoVisible = false
  LockPosition = false
  Perspective = false
  Rotation = 0
  RotationVector = (1,0,0)
  Scale = 2
  ScaleType = 2
  ScrubCount = 0
  SeamHidden = false
  SeamVisible = false
  SmoothHidden = false
  SmoothVisible = true
  Source = -> [Body001]
  Type = 5
  X = 0
  XDirection = (1,0,0)
  Y = -74.9174
FEATURE [TechDraw::DrawProjGroupItem] ProjItem008  label="Top001"
  CoarseView = false
  Direction = (0,1,0)
  Focus = 100
  HardHidden = false
  IsoCount = 0
  IsoHidden = false
  IsoVisible = false
  LockPosition = false
  Perspective = false
  Rotation = 0
  RotationVector = (1,0,0)
  Scale = 2
  ScaleType = 2
  ScrubCount = 0
  SeamHidden = false
  SeamVisible = false
  SmoothHidden = false
  SmoothVisible = true
  Source = -> [Body001]
  Type = 4
  X = 0
  XDirection = (1,0,0)
  Y = 74.9174
FEATURE [TechDraw::DrawProjGroupItem] ProjItem009  label="Right001"
  Caption = See section C
  CoarseView = false
  Direction = (1,0,1e-16)
  Focus = 100
  HardHidden = false
  IsoCount = 0
  IsoHidden = false
  IsoVisible = false
  LockPosition = false
  Perspective = false
  Rotation = 0
  RotationVector = (1,0,0)
  Scale = 2
  ScaleType = 2
  ScrubCount = 0
  SeamHidden = false
  SeamVisible = false
  SmoothHidden = false
  SmoothVisible = true
  Source = -> [Body001]
  Type = 2
  X = 101.118
  XDirection = (1e-16,0,-1)
  Y = 0
FEATURE [TechDraw::DrawProjGroupItem] ProjItem010  label="FrontTopRight"
  CoarseView = false
  Direction = (0.57735,0.57735,0.57735)
  Focus = 100
  HardHidden = false
  IsoCount = 0
  IsoHidden = false
  IsoVisible = false
  LockPosition = false
  Perspective = false
  Rotation = 0
  RotationVector = (1,0,0)
  Scale = 2
  ScaleType = 2
  ScrubCount = 0
  SeamHidden = false
  SeamVisible = false
  SmoothHidden = false
  SmoothVisible = true
  Source = -> [Body001]
  Type = 7
  X = 189.31
  XDirection = (0.707107,0,-0.707107)
  Y = 95.4536
FEATURE [TechDraw::DrawViewDimension] Dimension045
  AngleOverride = false
  Arbitrary = false
  ArbitraryTolerances = false
  EqualTolerance = true
  ExtensionAngle = 0
  FormatSpec = %.2w
  FormatSpecOverTolerance = %+.2w
  FormatSpecUnderTolerance = %+.2w
  Inverted = false
  LineAngle = 0
  LockPosition = false
  MeasureType = 1
  OverTolerance = 0
  References2D = -> [ProjItem008]
  Rotation = 0
  Scale = 2
  ScaleType = 0
  TheoreticalExact = false
  Type = 2
  UnderTolerance = 0
  X = -46.9422
  Y = 0.434362
FEATURE [TechDraw::DrawViewDimension] Dimension046
  AngleOverride = false
  Arbitrary = false
  ArbitraryTolerances = false
  EqualTolerance = true
  ExtensionAngle = 0
  FormatSpec = %.2w
  FormatSpecOverTolerance = %+.2w
  FormatSpecUnderTolerance = %+.2w
  Inverted = false
  LineAngle = 0
  LockPosition = false
  MeasureType = 1
  OverTolerance = 0
  References2D = -> [ProjItem008]
  Rotation = 0
  Scale = 2
  ScaleType = 0
  TheoreticalExact = false
  Type = 1
  UnderTolerance = 0
  X = -0.430785
  Y = 46.0365
FEATURE [TechDraw::DrawViewDimension] Dimension049
  AngleOverride = false
  Arbitrary = false
  ArbitraryTolerances = false
  EqualTolerance = true
  ExtensionAngle = 0
  FormatSpec = ⌀%.2w
  FormatSpecOverTolerance = %+.2w
  FormatSpecUnderTolerance = %+.2w
  Inverted = false
  LineAngle = 0
  LockPosition = false
  MeasureType = 1
  OverTolerance = 0
  References2D = -> [ProjItem007]
  Rotation = 0
  Scale = 2
  ScaleType = 0
  TheoreticalExact = false
  Type = 5
  UnderTolerance = 0
  X = -35.4853
  Y = 39.9334
FEATURE [TechDraw::DrawViewDimension] Dimension052
  AngleOverride = false
  Arbitrary = false
  ArbitraryTolerances = false
  EqualTolerance = true
  ExtensionAngle = 0
  FormatSpec = %.2w
  FormatSpecOverTolerance = %+.2w
  FormatSpecUnderTolerance = %+.2w
  Inverted = false
  LineAngle = 0
  LockPosition = false
  MeasureType = 1
  OverTolerance = 0
  References2D = -> [ProjItem009]
  Rotation = 0
  Scale = 2
  ScaleType = 0
  TheoreticalExact = false
  Type = 1
  UnderTolerance = 0
  X = -0.64789
  Y = -27.1179
FEATURE [TechDraw::DrawViewDimension] Dimension054
  AngleOverride = false
  Arbitrary = false
  ArbitraryTolerances = false
  EqualTolerance = true
  ExtensionAngle = 0
  FormatSpec = %.2w
  FormatSpecOverTolerance = %+.2w
  FormatSpecUnderTolerance = %+.2w
  Inverted = false
  LineAngle = 0
  LockPosition = false
  MeasureType = 1
  OverTolerance = 0
  References2D = -> [ProjItem006]
  Rotation = 0
  Scale = 2
  ScaleType = 0
  TheoreticalExact = false
  Type = 1
  UnderTolerance = 0
  X = 19.0982
  Y = -27.0239
FEATURE [TechDraw::DrawViewDimension] Dimension055
  AngleOverride = false
  Arbitrary = false
  ArbitraryTolerances = false
  EqualTolerance = true
  ExtensionAngle = 0
  FormatSpec = %.1w
  FormatSpecOverTolerance = %+.2w
  FormatSpecUnderTolerance = %+.2w
  Inverted = false
  LineAngle = 0
  LockPosition = false
  MeasureType = 1
  OverTolerance = 0
  References2D = -> [ProjItem006]
  Rotation = 0
  Scale = 2
  ScaleType = 0
  TheoreticalExact = false
  Type = 2
  UnderTolerance = 0
  X = -45.1906
  Y = 8.27165
FEATURE [TechDraw::DrawViewSection] SectionView002  label="Section C"
  BaseView = -> ProjItem009
  Caption = Scale 2:1
  CoarseView = false
  CutSurfaceDisplay = 2
  Direction = (-1e-16,-1e-16,1)
  FileGeomPattern = C:/Program Files/FreeCAD 0.21/data/Mod/TechDraw/PAT/FCPAT.pat
  FileHatchPattern = C:/Program Files/FreeCAD 0.21/data/Mod/TechDraw/Patterns/simple.svg
  Focus = 100
  FuseBeforeCut = false
  HardHidden = false
  HatchOffset = (0,0,0)
  HatchRotation = 0
  HatchScale = 1
  IsoCount = 0
  IsoHidden = false
  IsoVisible = false
  LockPosition = false
  NameGeomPattern = Diamond
  Perspective = false
  Rotation = -90
  Scale = 2
  ScaleType = 0
  ScrubCount = 0
  SeamHidden = false
  SeamVisible = false
  SectionDirection = 4
  SectionNormal = (-1e-16,-1e-16,1)
  SectionOrigin = (0,18.1,0)
  SmoothHidden = false
  SmoothVisible = true
  Source = -> [Body001]
  TrimAfterCut = false
  X = 64.6281
  XDirection = (0,-1,-1e-16)
  Y = 150.78
FEATURE [TechDraw::DrawProjGroupItem] ProjItem011  label="FrontBottomLeft"
  CoarseView = false
  Direction = (-0.57735,-0.57735,0.57735)
  Focus = 100
  HardHidden = false
  IsoCount = 0
  IsoHidden = false
  IsoVisible = false
  LockPosition = false
  Perspective = false
  Rotation = 0
  RotationVector = (1,0,0)
  Scale = 2
  ScaleType = 2
  ScrubCount = 0
  SeamHidden = false
  SeamVisible = false
  SmoothHidden = false
  SmoothVisible = true
  Source = -> [Body001]
  Type = 8
  X = -101.118
  XDirection = (0.707107,0,0.707107)
  Y = -74.4998
FEATURE [TechDraw::DrawProjGroup] ProjGroup001
  Anchor = -> ProjItem006
  AutoDistribute = true
  LockPosition = false
  ProjectionType = 1
  Rotation = 0
  Scale = 2
  ScaleType = 0
  Source = -> [Body001]
  Views = -> [ProjItem006,ProjItem007,ProjItem008,ProjItem009,ProjItem010,ProjItem011]
  X = 164.805
  Y = 144.542
  spacingX = 20
  spacingY = 25
FEATURE [TechDraw::DrawViewDetail] Detail  label="Detail A"
  AnchorPoint = (-14.69,-3.17,0)
  BaseView = -> SectionView002
  Caption = Scale 7:1
  CoarseView = false
  Direction = (-1e-16,-1e-16,1)
  Focus = 100
  HardHidden = false
  IsoCount = 0
  IsoHidden = false
  IsoVisible = false
  LockPosition = false
  Perspective = false
  Radius = 3
  Reference = A
  Rotation = 0
  Scale = 7
  ScaleType = 2
  ScrubCount = 0
  SeamHidden = false
  SeamVisible = false
  SmoothHidden = false
  SmoothVisible = true
  Source = -> [Body001]
  X = 60.7942
  XDirection = (0,-1,-1e-16)
  Y = 78.1992
FEATURE [TechDraw::DrawViewDimension] Dimension056
  AngleOverride = false
  Arbitrary = false
  ArbitraryTolerances = false
  EqualTolerance = true
  ExtensionAngle = 0
  FormatSpec = %.2w
  FormatSpecOverTolerance = %+.2w
  FormatSpecUnderTolerance = %+.2w
  Inverted = false
  LineAngle = 0
  LockPosition = false
  MeasureType = 1
  OverTolerance = 0
  References2D = -> [Detail]
  Rotation = 0
  Scale = 2
  ScaleType = 0
  TheoreticalExact = false
  Type = 2
  UnderTolerance = 0
  X = 28.1786
  Y = 19.7177
FEATURE [TechDraw::DrawViewDimension] Dimension058
  AngleOverride = false
  Arbitrary = false
  ArbitraryTolerances = false
  EqualTolerance = true
  ExtensionAngle = 0
  FormatSpec = %.2w
  FormatSpecOverTolerance = %+.2w
  FormatSpecUnderTolerance = %+.2w
  Inverted = false
  LineAngle = 0
  LockPosition = false
  MeasureType = 1
  OverTolerance = 0
  References2D = -> [Detail]
  Rotation = 0
  Scale = 2
  ScaleType = 0
  TheoreticalExact = false
  Type = 7
  UnderTolerance = 0
  X = -31.0787
  Y = -2.20467
FEATURE [TechDraw::DrawViewDimension] Dimension059
  AngleOverride = false
  Arbitrary = false
  ArbitraryTolerances = false
  EqualTolerance = true
  ExtensionAngle = 0
  FormatSpec = %.1w
  FormatSpecOverTolerance = %+.2w
  FormatSpecUnderTolerance = %+.2w
  Inverted = false
  LineAngle = 0
  LockPosition = false
  MeasureType = 1
  OverTolerance = 0
  References2D = -> [Detail]
  Rotation = 0
  Scale = 2
  ScaleType = 0
  TheoreticalExact = false
  Type = 0
  UnderTolerance = 0
  X = -11.5812
  Y = 32.7486
FEATURE [TechDraw::DrawViewDimension] Dimension060
  AngleOverride = false
  Arbitrary = false
  ArbitraryTolerances = false
  EqualTolerance = true
  ExtensionAngle = 0
  FormatSpec = R%.2w
  FormatSpecOverTolerance = %+.2w
  FormatSpecUnderTolerance = %+.2w
  Inverted = false
  LineAngle = 0
  LockPosition = false
  MeasureType = 1
  OverTolerance = 0
  References2D = -> [ProjItem006]
  Rotation = 0
  Scale = 2
  ScaleType = 0
  TheoreticalExact = false
  Type = 4
  UnderTolerance = 0
  X = -43.3707
  Y = 22.8443
FEATURE [TechDraw::DrawViewDimension] Dimension063
  AngleOverride = false
  Arbitrary = false
  ArbitraryTolerances = false
  EqualTolerance = true
  ExtensionAngle = 0
  FormatSpec = %.2w
  FormatSpecOverTolerance = %+.2w
  FormatSpecUnderTolerance = %+.2w
  Inverted = false
  LineAngle = 0
  LockPosition = false
  MeasureType = 1
  OverTolerance = 0
  References2D = -> [ProjItem009]
  Rotation = 0
  Scale = 2
  ScaleType = 0
  TheoreticalExact = false
  Type = 2
  UnderTolerance = 0
  X = 39.7437
  Y = -22.5045
FEATURE [TechDraw::DrawSVGTemplate] Template002
  EditableTexts = AuthorName=Alex Anastasakis; CheckDate=2024/11/11; CreationDate=2024/11/10; DrawingNumber=6; FC-Scale=3:1; FC-Title=Pusher; SheetNumber=1 of 1; Subtitle=Course: Industrial Design for Game Hardware; SupervisorName=Alvaro Uribe Quevedo; Weight=0.004
  Height = 297
  Orientation = 1
  Template = C:/Program Files/FreeCAD 0.21/data/Mod/TechDraw/Templates/A3_LandscapeTD.svg
  Width = 420
FEATURE [TechDraw::DrawProjGroupItem] ProjItem012  label="Front002"
  CoarseView = false
  Direction = (0,0,1)
  Focus = 100
  HardHidden = false
  IsoCount = 0
  IsoHidden = false
  IsoVisible = false
  LockPosition = true
  Perspective = false
  Rotation = 0
  RotationVector = (1,0,0)
  Scale = 3
  ScaleType = 2
  ScrubCount = 0
  SeamHidden = false
  SeamVisible = false
  SmoothHidden = false
  SmoothVisible = true
  Source = -> [Body012]
  Type = 0
  X = 0
  XDirection = (1,0,0)
  Y = 0
FEATURE [TechDraw::DrawProjGroupItem] ProjItem016  label="FrontTopRight001"
  CoarseView = false
  Direction = (0.57735,0.57735,0.57735)
  Focus = 100
  HardHidden = false
  IsoCount = 0
  IsoHidden = false
  IsoVisible = false
  LockPosition = false
  Perspective = false
  Rotation = 0
  RotationVector = (1,0,0)
  Scale = 3
  ScaleType = 2
  ScrubCount = 0
  SeamHidden = false
  SeamVisible = false
  SmoothHidden = false
  SmoothVisible = true
  Source = -> [Body012]
  Type = 7
  X = 132.574
  XDirection = (0.707107,0,-0.707107)
  Y = 46.4
FEATURE [TechDraw::DrawViewDimension] Dimension064
  AngleOverride = false
  Arbitrary = false
  ArbitraryTolerances = false
  EqualTolerance = true
  ExtensionAngle = 0
  FormatSpec = %.2w
  FormatSpecOverTolerance = %+.2w
  FormatSpecUnderTolerance = %+.2w
  Inverted = false
  LineAngle = 0
  LockPosition = false
  MeasureType = 1
  OverTolerance = 0
  References2D = -> [ProjItem012]
  Rotation = 0
  Scale = 3
  ScaleType = 0
  TheoreticalExact = false
  Type = 2
  UnderTolerance = 0
  X = -43.2432
  Y = 27.4359
FEATURE [TechDraw::DrawViewDimension] Dimension067
  AngleOverride = false
  Arbitrary = false
  ArbitraryTolerances = false
  EqualTolerance = true
  ExtensionAngle = 0
  FormatSpec = R%.2w
  FormatSpecOverTolerance = %+.2w
  FormatSpecUnderTolerance = %+.2w
  Inverted = false
  LineAngle = 0
  LockPosition = false
  MeasureType = 1
  OverTolerance = 0
  References2D = -> [ProjItem012]
  Rotation = 0
  Scale = 3
  ScaleType = 0
  TheoreticalExact = false
  Type = 4
  UnderTolerance = 0
  X = 11.3232
  Y = 37.0228
FEATURE [TechDraw::DrawViewDimension] Dimension068
  AngleOverride = false
  Arbitrary = false
  ArbitraryTolerances = false
  EqualTolerance = true
  ExtensionAngle = 0
  FormatSpec = R%.2w
  FormatSpecOverTolerance = %+.2w
  FormatSpecUnderTolerance = %+.2w
  Inverted = false
  LineAngle = 0
  LockPosition = false
  MeasureType = 1
  OverTolerance = 0
  References2D = -> [ProjItem012]
  Rotation = 0
  Scale = 3
  ScaleType = 0
  TheoreticalExact = false
  Type = 4
  UnderTolerance = 0
  X = -31.0444
  Y = 37.183
FEATURE [TechDraw::DrawViewDimension] Dimension070
  AngleOverride = false
  Arbitrary = false
  ArbitraryTolerances = false
  EqualTolerance = true
  ExtensionAngle = 0
  FormatSpec = %.2w
  FormatSpecOverTolerance = %+.2w
  FormatSpecUnderTolerance = %+.2w
  Inverted = false
  LineAngle = 0
  LockPosition = false
  MeasureType = 1
  OverTolerance = 0
  References2D = -> [ProjItem012]
  Rotation = 0
  Scale = 3
  ScaleType = 0
  TheoreticalExact = false
  Type = 1
  UnderTolerance = 0
  X = 15.0038
  Y = -29.7883
FEATURE [TechDraw::DrawViewDimension] Dimension072
  AngleOverride = false
  Arbitrary = false
  ArbitraryTolerances = false
  EqualTolerance = true
  ExtensionAngle = 0
  FormatSpec = %.2w
  FormatSpecOverTolerance = %+.2w
  FormatSpecUnderTolerance = %+.2w
  Inverted = false
  LineAngle = 0
  LockPosition = false
  MeasureType = 1
  OverTolerance = 0
  References2D = -> [ProjItem012]
  Rotation = 0
  Scale = 3
  ScaleType = 0
  TheoreticalExact = false
  Type = 2
  UnderTolerance = 0
  X = 45.0742
  Y = 10.4193
FEATURE [TechDraw::DrawViewDimension] Dimension073
  AngleOverride = false
  Arbitrary = false
  ArbitraryTolerances = false
  EqualTolerance = true
  ExtensionAngle = 0
  FormatSpec = %.2w
  FormatSpecOverTolerance = %+.2w
  FormatSpecUnderTolerance = %+.2w
  Inverted = false
  LineAngle = 0
  LockPosition = false
  MeasureType = 1
  OverTolerance = 0
  References2D = -> [ProjItem012]
  Rotation = 0
  Scale = 3
  ScaleType = 0
  TheoreticalExact = false
  Type = 2
  UnderTolerance = 0
  X = 49.3075
  Y = -0.500001
FEATURE [TechDraw::DrawViewDimension] Dimension075
  AngleOverride = false
  Arbitrary = false
  ArbitraryTolerances = false
  EqualTolerance = true
  ExtensionAngle = 0
  FormatSpec = %.2w
  FormatSpecOverTolerance = %+.2w
  FormatSpecUnderTolerance = %+.2w
  Inverted = false
  LineAngle = 0
  LockPosition = false
  MeasureType = 1
  OverTolerance = 0
  References2D = -> [ProjItem012]
  Rotation = 0
  Scale = 3
  ScaleType = 0
  TheoreticalExact = false
  Type = 6
  UnderTolerance = 0
  X = -46.8223
  Y = -10.0706
FEATURE [TechDraw::DrawProjGroupItem] ProjItem017  label="Bottom001"
  CoarseView = false
  Direction = (0,-1,0)
  Focus = 100
  HardHidden = false
  IsoCount = 0
  IsoHidden = false
  IsoVisible = false
  LockPosition = false
  Perspective = false
  Rotation = 0
  RotationVector = (1,0,0)
  Scale = 3
  ScaleType = 2
  ScrubCount = 0
  SeamHidden = false
  SeamVisible = false
  SmoothHidden = false
  SmoothVisible = true
  Source = -> [Body012]
  Type = 5
  X = 0
  XDirection = (1,0,0)
  Y = -84.9378
FEATURE [TechDraw::DrawProjGroup] ProjGroup002
  Anchor = -> ProjItem012
  AutoDistribute = false
  LockPosition = false
  ProjectionType = 1
  Rotation = 0
  Scale = 3
  ScaleType = 0
  Source = -> [Body012]
  Views = -> [ProjItem012,ProjItem016,ProjItem017]
  X = 147.874
  Y = 161.882
  spacingX = 20
  spacingY = 20
FEATURE [TechDraw::DrawViewDimension] Dimension076
  AngleOverride = false
  Arbitrary = false
  ArbitraryTolerances = false
  EqualTolerance = true
  ExtensionAngle = 0
  FormatSpec = %.2w x45°
  FormatSpecOverTolerance = %+.2w
  FormatSpecUnderTolerance = %+.2w
  Inverted = false
  LineAngle = 0
  LockPosition = false
  MeasureType = 1
  OverTolerance = 0
  References2D = -> [ProjItem017]
  Rotation = 0
  Scale = 3
  ScaleType = 0
  TheoreticalExact = false
  Type = 2
  UnderTolerance = 0
  X = 45.3739
  Y = -12.0366
FEATURE [TechDraw::DrawViewDimension] Dimension077
  AngleOverride = false
  Arbitrary = false
  ArbitraryTolerances = false
  EqualTolerance = true
  ExtensionAngle = 0
  FormatSpec = ⌀%.2w
  FormatSpecOverTolerance = %+.2w
  FormatSpecUnderTolerance = %+.2w
  Inverted = false
  LineAngle = 0
  LockPosition = false
  MeasureType = 1
  OverTolerance = 0
  References2D = -> [ProjItem017]
  Rotation = 0
  Scale = 3
  ScaleType = 0
  TheoreticalExact = false
  Type = 5
  UnderTolerance = 0
  X = 50.9146
  Y = 33.5585
FEATURE [TechDraw::DrawViewDimension] Dimension079
  AngleOverride = false
  Arbitrary = false
  ArbitraryTolerances = false
  EqualTolerance = true
  ExtensionAngle = 0
  FormatSpec = %.1w
  FormatSpecOverTolerance = %+.2w
  FormatSpecUnderTolerance = %+.2w
  Inverted = false
  LineAngle = 0
  LockPosition = false
  MeasureType = 1
  OverTolerance = 0
  References2D = -> [ProjItem012]
  Rotation = 0
  Scale = 3
  ScaleType = 0
  TheoreticalExact = false
  Type = 1
  UnderTolerance = 0
  X = -13.2822
  Y = 30.3187
FEATURE [TechDraw::DrawSVGTemplate] Template003
  EditableTexts = AuthorName=Alex Anastasakis; CheckDate=2024/11/11; CreationDate=2024/11/10; DrawingNumber=9; FC-Scale=4:1; FC-Title=Plug; SheetNumber=1 of 1; Subtitle=Course: Industrial Design for Game Hardware; SupervisorName=Alvaro Uribe Quevedo; Weight=0.002
  Height = 297
  Orientation = 1
  Template = C:/Program Files/FreeCAD 0.21/data/Mod/TechDraw/Templates/A3_LandscapeTD.svg
  Width = 420
FEATURE [PartDesign::Draft] Draft
  Angle = 2
  Base = -> Pad015 [Face1]
  BaseFeature = -> Pad015
  NeutralPlane = -> Pad015 [Face3]
  Placement = pos=(0,0,0) rot=(1,0,0;1.5708rad)
  SupportTransform = false
FEATURE [PartDesign::Body] Body013  label="WirePlug"
  Group = -> [Sketch026,Pad015,Draft]
  Origin = -> Origin013
  Placement = pos=(0,-190,0) rot=(0,0,1;0rad)
  Tip = -> Draft
FEATURE [TechDraw::DrawProjGroupItem] ProjItem018  label="Front003"
  CoarseView = false
  Direction = (1,0,0)
  Focus = 100
  HardHidden = true
  IsoCount = 0
  IsoHidden = false
  IsoVisible = false
  LockPosition = true
  Perspective = false
  Rotation = 0
  RotationVector = (0,0,-1)
  Scale = 4
  ScaleType = 2
  ScrubCount = 0
  SeamHidden = false
  SeamVisible = false
  SmoothHidden = false
  SmoothVisible = true
  Source = -> [Body013]
  Type = 0
  X = 0
  XDirection = (0,0,-1)
  Y = 0
FEATURE [TechDraw::DrawProjGroupItem] ProjItem019  label="Top002"
  CoarseView = false
  Direction = (0,1,0)
  Focus = 100
  HardHidden = false
  IsoCount = 0
  IsoHidden = false
  IsoVisible = false
  LockPosition = false
  Perspective = false
  Rotation = 0
  RotationVector = (1,0,0)
  Scale = 4
  ScaleType = 2
  ScrubCount = 0
  SeamHidden = false
  SeamVisible = false
  SmoothHidden = false
  SmoothVisible = true
  Source = -> [Body013]
  Type = 4
  X = 0
  XDirection = (0,0,-1)
  Y = 116.27
FEATURE [TechDraw::DrawProjGroupItem] ProjItem020  label="FrontTopRight002"
  CoarseView = false
  Direction = (0.57735,0.57735,-0.57735)
  Focus = 100
  HardHidden = true
  IsoCount = 0
  IsoHidden = false
  IsoVisible = false
  LockPosition = false
  Perspective = false
  Rotation = 0
  RotationVector = (1,0,0)
  Scale = 4
  ScaleType = 2
  ScrubCount = 0
  SeamHidden = false
  SeamVisible = false
  SmoothHidden = false
  SmoothVisible = true
  Source = -> [Body013]
  Type = 7
  X = 134.544
  XDirection = (-0.707107,0,-0.707107)
  Y = 118.249
FEATURE [TechDraw::DrawProjGroup] ProjGroup003
  Anchor = -> ProjItem018
  AutoDistribute = false
  LockPosition = false
  ProjectionType = 1
  Rotation = 0
  Scale = 4
  ScaleType = 0
  Source = -> [Body013]
  Views = -> [ProjItem018,ProjItem019,ProjItem020]
  X = 143.246
  Y = 88.3693
  spacingX = 30
  spacingY = 20
FEATURE [TechDraw::DrawViewDimension] Dimension080
  AngleOverride = false
  Arbitrary = false
  ArbitraryTolerances = false
  EqualTolerance = true
  ExtensionAngle = 0
  FormatSpec = ⌀%.2w
  FormatSpecOverTolerance = %+.2w
  FormatSpecUnderTolerance = %+.2w
  Inverted = false
  LineAngle = 0
  LockPosition = false
  MeasureType = 1
  OverTolerance = 0
  References2D = -> [ProjItem019]
  Rotation = 0
  Scale = 4
  ScaleType = 0
  TheoreticalExact = false
  Type = 5
  UnderTolerance = 0
  X = -57.7215
  Y = 31.3435
FEATURE [TechDraw::DrawViewDimension] Dimension081
  AngleOverride = false
  Arbitrary = false
  ArbitraryTolerances = false
  EqualTolerance = true
  ExtensionAngle = 0
  FormatSpec = ⌀%.2w
  FormatSpecOverTolerance = %+.2w
  FormatSpecUnderTolerance = %+.2w
  Inverted = false
  LineAngle = 0
  LockPosition = false
  MeasureType = 1
  OverTolerance = 0
  References2D = -> [ProjItem019]
  Rotation = 0
  Scale = 4
  ScaleType = 0
  TheoreticalExact = false
  Type = 5
  UnderTolerance = 0
  X = 51.5373
  Y = 46.1416
FEATURE [TechDraw::DrawViewDimension] Dimension083
  AngleOverride = false
  Arbitrary = false
  ArbitraryTolerances = false
  EqualTolerance = true
  ExtensionAngle = 0
  FormatSpec = %.2w
  FormatSpecOverTolerance = %+.2w
  FormatSpecUnderTolerance = %+.2w
  Inverted = false
  LineAngle = 0
  LockPosition = false
  MeasureType = 1
  OverTolerance = 0
  References2D = -> [ProjItem018]
  Rotation = 0
  Scale = 4
  ScaleType = 0
  TheoreticalExact = false
  Type = 6
  UnderTolerance = 0
  X = 52.0143
  Y = 31.509
FEATURE [TechDraw::DrawViewDimension] Dimension084
  AngleOverride = false
  Arbitrary = false
  ArbitraryTolerances = false
  EqualTolerance = true
  ExtensionAngle = 0
  FormatSpec = %.2w
  FormatSpecOverTolerance = %+.2w
  FormatSpecUnderTolerance = %+.2w
  Inverted = false
  LineAngle = 0
  LockPosition = false
  MeasureType = 1
  OverTolerance = 0
  References2D = -> [ProjItem009]
  Rotation = 0
  Scale = 2
  ScaleType = 0
  TheoreticalExact = false
  Type = 2
  UnderTolerance = 0
  X = 11.831
  Y = -21.7206
FEATURE [TechDraw::DrawViewDimension] Dimension085
  AngleOverride = false
  Arbitrary = false
  ArbitraryTolerances = false
  EqualTolerance = true
  ExtensionAngle = 0
  FormatSpec = %.2w
  FormatSpecOverTolerance = %+.2w
  FormatSpecUnderTolerance = %+.2w
  Inverted = false
  LineAngle = 0
  LockPosition = false
  MeasureType = 1
  OverTolerance = 0
  References2D = -> [ProjItem009]
  Rotation = 0
  Scale = 2
  ScaleType = 0
  TheoreticalExact = false
  Type = 2
  UnderTolerance = 0
  X = 47.4106
  Y = -29.8841
FEATURE [TechDraw::DrawViewDimension] Dimension086
  AngleOverride = false
  Arbitrary = false
  ArbitraryTolerances = false
  EqualTolerance = true
  ExtensionAngle = 0
  FormatSpec = %.2w x45°
  FormatSpecOverTolerance = %+.2w
  FormatSpecUnderTolerance = %+.2w
  Inverted = false
  LineAngle = 0
  LockPosition = false
  MeasureType = 1
  OverTolerance = 0
  References2D = -> [ProjItem017]
  Rotation = 0
  Scale = 3
  ScaleType = 0
  TheoreticalExact = false
  Type = 1
  UnderTolerance = 0
  X = 18.5222
  Y = -45.2779
FEATURE [TechDraw::DrawViewDimension] Dimension087
  AngleOverride = false
  Arbitrary = false
  ArbitraryTolerances = false
  EqualTolerance = true
  ExtensionAngle = 0
  FormatSpec = %.0w
  FormatSpecOverTolerance = %+.2w
  FormatSpecUnderTolerance = %+.2w
  Inverted = false
  LineAngle = 0
  LockPosition = false
  MeasureType = 1
  OverTolerance = 0
  References2D = -> [Detail]
  Rotation = 0
  Scale = 2
  ScaleType = 0
  TheoreticalExact = false
  Type = 7
  UnderTolerance = 0
  X = -19.8959
  Y = -17.4108
FEATURE [TechDraw::DrawPage] Page001  label="TopDrawing"
  KeepUpdated = true
  NextBalloonIndex = 3
  ProjectionType = 1
  Scale = 2
  Template = -> Template001
  Views = -> [ProjGroup001,Dimension045,Dimension046,Dimension049,Dimension052,Dimension054,Dimension055,SectionView002,Detail,Dimension056,Dimension058,Dimension059,Dimension060,Dimension063,Dimension084,Dimension085,Dimension087]
FEATURE [TechDraw::DrawViewDimension] Dimension088
  AngleOverride = false
  Arbitrary = false
  ArbitraryTolerances = false
  EqualTolerance = true
  ExtensionAngle = 0
  FormatSpec = %.2w
  FormatSpecOverTolerance = %+.2w
  FormatSpecUnderTolerance = %+.2w
  Inverted = false
  LineAngle = 0
  LockPosition = false
  MeasureType = 1
  OverTolerance = 0
  References2D = -> [ProjItem017]
  Rotation = 0
  Scale = 3
  ScaleType = 0
  TheoreticalExact = false
  Type = 2
  UnderTolerance = 0
  X = -55.707
  Y = 2.84174
FEATURE [TechDraw::DrawViewDimension] Dimension089
  AngleOverride = false
  Arbitrary = false
  ArbitraryTolerances = false
  EqualTolerance = true
  ExtensionAngle = 0
  FormatSpec = %.2w
  FormatSpecOverTolerance = %+.2w
  FormatSpecUnderTolerance = %+.2w
  Inverted = false
  LineAngle = 0
  LockPosition = false
  MeasureType = 1
  OverTolerance = 0
  References2D = -> [ProjItem017]
  Rotation = 0
  Scale = 3
  ScaleType = 0
  TheoreticalExact = false
  Type = 1
  UnderTolerance = 0
  X = 1.02522
  Y = -52.9008
FEATURE [TechDraw::DrawViewDimension] Dimension090
  AngleOverride = false
  Arbitrary = false
  ArbitraryTolerances = false
  EqualTolerance = true
  ExtensionAngle = 0
  FormatSpec = %.2w
  FormatSpecOverTolerance = %+.2w
  FormatSpecUnderTolerance = %+.2w
  Inverted = false
  LineAngle = 0
  LockPosition = false
  MeasureType = 1
  OverTolerance = 0
  References2D = -> [ProjItem012]
  Rotation = 0
  Scale = 3
  ScaleType = 0
  TheoreticalExact = false
  Type = 2
  UnderTolerance = 0
  X = 40.4937
  Y = -14.2166
FEATURE [TechDraw::DrawPage] Page002  label="PusherDrawing"
  KeepUpdated = true
  NextBalloonIndex = 3
  ProjectionType = 1
  Scale = 3
  Template = -> Template002
  Views = -> [ProjGroup002,Dimension064,Dimension067,Dimension068,Dimension070,Dimension072,Dimension073,Dimension075,Dimension076,Dimension077,Dimension079,Dimension086,Dimension088,Dimension089,Dimension090]
FEATURE [TechDraw::DrawViewDimension] Dimension091
  AngleOverride = false
  Arbitrary = false
  ArbitraryTolerances = false
  EqualTolerance = true
  ExtensionAngle = 0
  FormatSpec = %.2w
  FormatSpecOverTolerance = %+.2w
  FormatSpecUnderTolerance = %+.2w
  Inverted = false
  LineAngle = 0
  LockPosition = false
  MeasureType = 1
  OverTolerance = 0
  References2D = -> [ProjItem018]
  Rotation = 0
  Scale = 4
  ScaleType = 0
  TheoreticalExact = false
  Type = 2
  UnderTolerance = 0
  X = -59.9098
  Y = 2.5
FEATURE [TechDraw::DrawPage] Page003  label="PlugDrawing"
  KeepUpdated = true
  NextBalloonIndex = 4
  ProjectionType = 1
  Scale = 4
  Template = -> Template003
  Views = -> [ProjGroup003,Dimension080,Dimension081,Dimension083,Dimension091]
FEATURE [App::DocumentObjectGroupPython] ExplodedAssembly  # scripted group (container) (typed FeaturePython)
  AnimationStep = 0
  CurrentTrajectory = 0
  InAnimation = false
  RemoveAllTrajectories = false
  ResetAnimation = false
FEATURE [App::Link] Body_CutLink
  LinkTransform = true
  LinkedObject = -> Body
FEATURE [App::Link] Body001_CutLink
  LinkTransform = true
  LinkedObject = -> Body001
FEATURE [App::Link] Body002_CutLink
  LinkTransform = true
  LinkedObject = -> Body002
FEATURE [App::Link] Body003_CutLink
  LinkTransform = true
  LinkedObject = -> Body003
FEATURE [App::Link] Body005_CutLink
  LinkTransform = true
  LinkedObject = -> Body005
FEATURE [App::Link] Body006_CutLink
  LinkTransform = true
  LinkedObject = -> Body006
FEATURE [App::Link] Body007_CutLink
  LinkTransform = true
  LinkedObject = -> Body007
FEATURE [App::Link] Body008_CutLink
  LinkTransform = true
  LinkedObject = -> Body008
FEATURE [App::Link] Body009_CutLink
  LinkTransform = true
  LinkedObject = -> Body009
FEATURE [App::Link] Body010_CutLink
  LinkTransform = true
  LinkedObject = -> Body010
FEATURE [App::Link] Body011_CutLink
  LinkTransform = true
  LinkedObject = -> Body011
FEATURE [App::Link] Body012_CutLink
  LinkTransform = true
  LinkedObject = -> Body012
FEATURE [App::Link] Body013_CutLink
  LinkTransform = true
  LinkedObject = -> Body013
FEATURE [Part::FeaturePython] SectionCutCompound  # WARN: FeaturePython — macro-defined, semantics opaque (R4)
  Mode = 0
  Objects = -> [Body_CutLink,Body001_CutLink,Body002_CutLink,Body003_CutLink,Body005_CutLink,Body006_CutLink,Body007_CutLink,Body008_CutLink,Body009_CutLink,Body010_CutLink,Body011_CutLink,Body012_CutLink,Body013_CutLink]
  Tolerance = 0
FEATURE [Part::Box] SectionCutBoxX
  AttacherType = Attacher::AttachEngine3D
  Height = 117
  Length = 111
  Placement = pos=(0,-200.5,-58.5) rot=(0,0,1;0rad)
  Width = 256
FEATURE [Part::Cut] SectionCutX
  Base = -> SectionCutCompound
  Tool = -> SectionCutBoxX
FEATURE [Sketcher::SketchObject] Sketch027
  FullyConstrained = true
  MapMode = 5
  Placement = pos=(0,0,0) rot=(1,0,0;1.5708rad)
  Support = -> [XZ_Plane002]
  sketch-geometry (5):
    g0: LineSegment StartX=-0.5 StartY=-45 StartZ=0 EndX=-0.5 EndY=45 EndZ=0
    g1: LineSegment StartX=-0.5 StartY=45 StartZ=0 EndX=0.5 EndY=45 EndZ=0
    g2: LineSegment StartX=0.5 StartY=45 StartZ=0 EndX=0.5 EndY=-45 EndZ=0
    g3: LineSegment StartX=0.5 StartY=-45 StartZ=0 EndX=-0.5 EndY=-45 EndZ=0
    g4: GeomPoint X=0 Y=0 Z=0
  constraints (12):
    c: Coincident(g0,g1)
    c: Coincident(g1,g2)
    c: Coincident(g2,g3)
    c: Coincident(g3,g0)
    c: Horizontal(g1)
    c: Horizontal(g3)
    c: Vertical(g0)
    c: Vertical(g2)
    c: Symmetric(g1,g0,g4)
    c: Coincident(g4,g-1)
    c: DistanceX(g1,g1) = 1
    c: DistanceY(g2,g2) = 90
FEATURE [PartDesign::Pocket] Pocket012
  BaseFeature = -> Pocket007
  Direction = (0,1,2e-16)
  Length = 5
  Length2 = 5
  Profile = -> Sketch027
  ReferenceAxis = -> Sketch027 [N_Axis]
  Reversed = true
  Type = 1
FEATURE [PartDesign::Body] Body002  label="PVCHammerHeadShell"
  Group = -> [Sketch009,Pad002,Sketch010,Pocket007,Sketch027,Pocket012]
  Origin = -> Origin002
  Tip = -> Pocket012
FEATURE [App::DocumentObjectGroup] Group  label="Non3DPrints"
  Group = -> [Body007,Body006,Body005,Body003,Body002,Body008,Body009,Body010,Body011]
FEATURE [TechDraw::DrawViewDimension] Dimension039
  AngleOverride = false
  Arbitrary = false
  ArbitraryTolerances = false
  EqualTolerance = true
  ExtensionAngle = 0
  FormatSpec = %.2w x45°
  FormatSpecOverTolerance = %+.2w
  FormatSpecUnderTolerance = %+.2w
  Inverted = false
  LineAngle = 0
  LockPosition = false
  MeasureType = 1
  OverTolerance = 0
  References2D = -> [SectionView]
  Rotation = 0
  ScaleType = 0
  TheoreticalExact = false
  Type = 2
  UnderTolerance = 0
  X = -56.0497
  Y = 31.6953
FEATURE [TechDraw::DrawPage] Page  label="HeadDrawing"
  KeepUpdated = true
  NextBalloonIndex = 1
  ProjectionType = 1
  Template = -> Template
  Views = -> [ProjGroup,Dimension002,Dimension012,Dimension014,SectionView,SectionView001,Dimension017,Dimension021,Dimension022,Dimension023,Dimension024,Dimension029,Dimension030,Dimension031,Dimension032,Dimension033,Dimension034,Dimension035,Dimension036,Dimension037,Dimension038,Dimension039,Dimension,Dimension040,Dimension041,Dimension042,Dimension043,Dimension044]
